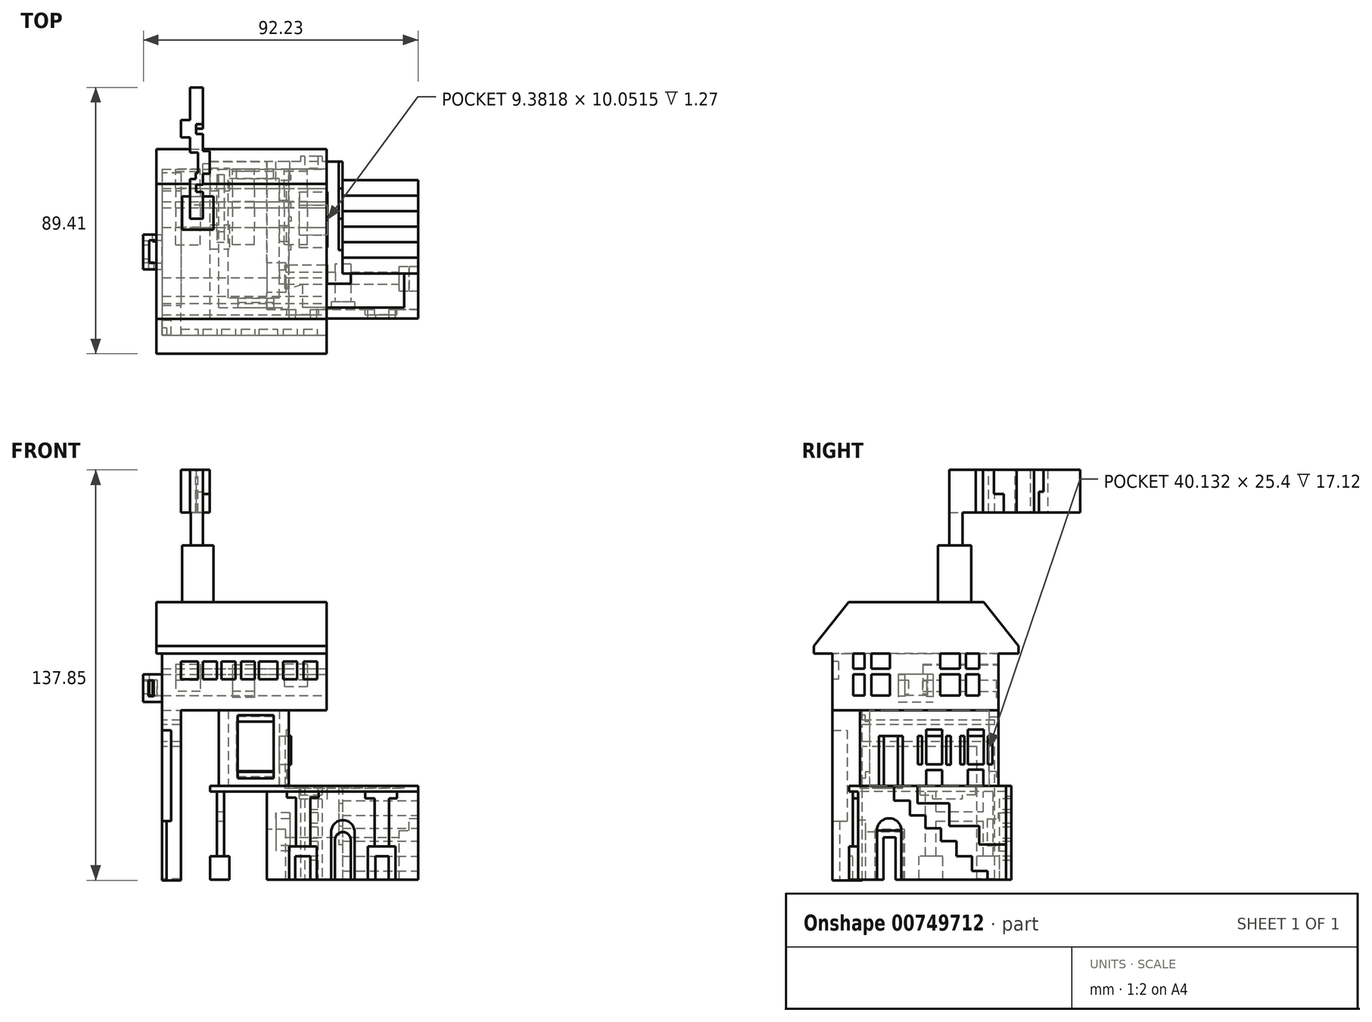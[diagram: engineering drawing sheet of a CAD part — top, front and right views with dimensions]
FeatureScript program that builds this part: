
annotation { "Feature Type Name" : "Feature", "Feature Type Description" : "" }
export const myFeature = defineFeature(function(context is Context, id is Id, definition is map)
    precondition{}
    {
        {
            var Q0;
            Q0=qCreatedBy(makeId("Right.planeOp"),FACE);
            var sketch = newSketch(context, id + "F0", { "sketchPlane" : qUnion([Q0])});
            skLineSegment(sketch, "E0.bottom", {"start": v(-30.5, 23.62) * mm, "end": v(19.16, 23.62) * mm});
            skLineSegment(sketch, "E0.top", {"start": v(-30.5, -7.94) * mm, "end": v(19.16, -7.94) * mm});
            skLineSegment(sketch, "E0.left", {"start": v(-30.5, 23.62) * mm, "end": v(-30.5, -7.94) * mm});
            skLineSegment(sketch, "E0.right", {"start": v(19.16, 23.62) * mm, "end": v(19.16, -7.94) * mm});
            skSolve(sketch);
        }
        {
            var Q0;
            Q0 = qSketchRegion(id + "F0", true);
            extrude(context, id + "F1", {"entities" : qUnion([Q0]), "depth" : 50.8 * mm, "offsetDistance" : 25.4 * mm});
        }
        {
            var Q0;
            Q0=makeQuery(id+"F1.opExtrude","CAP_FACE",FACE,{"disambiguationData":[OSD([sQuery(id+"F0.wireOp",EDGE,"E0.bottom"),sQuery(id+"F0.wireOp",EDGE,"E0.top"),sQuery(id+"F0.wireOp",EDGE,"E0.left"),sQuery(id+"F0.wireOp",EDGE,"E0.right")])],"isStart":false});
            var sketch = newSketch(context, id + "F2", { "sketchPlane" : qUnion([Q0])});
            skLineSegment(sketch, "E1", {"start": v(-18.43, 23.62) * mm, "end": v(-18.43, 18.63) * mm});
            skLineSegment(sketch, "E2", {"start": v(-18.43, 18.63) * mm, "end": v(-13.2, 18.63) * mm});
            skLineSegment(sketch, "E3", {"start": v(-13.2, 18.63) * mm, "end": v(-13.2, 13.64) * mm});
            skLineSegment(sketch, "E4", {"start": v(-13.2, 13.64) * mm, "end": v(-7.98, 13.64) * mm});
            skLineSegment(sketch, "E5", {"start": v(-7.98, 13.64) * mm, "end": v(-7.98, 9.31) * mm});
            skLineSegment(sketch, "E6", {"start": v(-7.98, 9.31) * mm, "end": v(-2.75, 9.31) * mm});
            skLineSegment(sketch, "E7", {"start": v(-2.75, 9.31) * mm, "end": v(-2.75, 5) * mm});
            skLineSegment(sketch, "E8", {"start": v(-2.75, 5) * mm, "end": v(2.48, 5) * mm});
            skLineSegment(sketch, "E9", {"start": v(2.48, 5) * mm, "end": v(2.48, 0) * mm});
            skLineSegment(sketch, "E10", {"start": v(2.48, 0) * mm, "end": v(7.7, 0) * mm});
            skLineSegment(sketch, "E11", {"start": v(7.7, 0) * mm, "end": v(7.7, -5) * mm});
            skLineSegment(sketch, "E12", {"start": v(7.7, -5) * mm, "end": v(12.93, -5) * mm});
            skLineSegment(sketch, "E13", {"start": v(12.93, -5) * mm, "end": v(12.93, -7.94) * mm});
            skLineSegment(sketch, "E14", {"start": v(12.93, -7.94) * mm, "end": v(19.16, -7.94) * mm});
            skSolve(sketch);
        }
        {
            var Q0;
            Q0 = qSketchRegion(id + "F2", true);
            var Q1;
            {var subQ0=sQuery(id+"F2.wireOp",EDGE,"E1");Q1=makeQuery(id+"F2.imprint","IMPRINT",FACE,{"disambiguationData":[TD([[makeQuery(id+"F2.imprint","IMPRINT",EDGE,{"derivedFrom":subQ0}),1.0]])]});}
            extrude(context, id + "F3", {"entities" : qUnion([Q0, Q1]), "operationType" : NewBodyOperationType.REMOVE, "oppositeDirection" : true, "depth" : 25.4 * mm, "offsetDistance" : 25.4 * mm});
        }
        {
            var Q0;
            Q0=makeQuery(id+"F1.opExtrude","CAP_FACE",FACE,{"disambiguationData":[OSD([sQuery(id+"F0.wireOp",EDGE,"E0.bottom"),sQuery(id+"F0.wireOp",EDGE,"E0.top"),sQuery(id+"F0.wireOp",EDGE,"E0.left"),sQuery(id+"F0.wireOp",EDGE,"E0.right")])],"isStart":false});
            var sketch = newSketch(context, id + "F4", { "sketchPlane" : qUnion([Q0])});
            skLineSegment(sketch, "E15.bottom", {"start": v(-24.26, -7.94) * mm, "end": v(-16.02, -7.94) * mm});
            skLineSegment(sketch, "E15.top", {"start": v(-24.26, 8.54) * mm, "end": v(-16.02, 8.54) * mm});
            skLineSegment(sketch, "E15.left", {"start": v(-24.26, -7.94) * mm, "end": v(-24.26, 8.54) * mm});
            skLineSegment(sketch, "E15.right", {"start": v(-16.02, -7.94) * mm, "end": v(-16.02, 8.54) * mm});
            skSolve(sketch);
        }
        {
            var Q0;
            Q0 = qSketchRegion(id + "F4", true);
            extrude(context, id + "F5", {"entities" : qUnion([Q0]), "operationType" : NewBodyOperationType.REMOVE, "oppositeDirection" : true, "depth" : 6.35 * mm, "offsetDistance" : 25.4 * mm});
        }
        {
            var Q0;
            Q0=makeQuery(id+"F5.boolean.opBoolean","COPY",FACE,{"derivedFrom":makeQuery(id+"F5.opExtrude","CAP_FACE",FACE,{"disambiguationData":[OSD([sQuery(id+"F4.wireOp",EDGE,"E15.bottom"),sQuery(id+"F4.wireOp",EDGE,"E15.top"),sQuery(id+"F4.wireOp",EDGE,"E15.left"),sQuery(id+"F4.wireOp",EDGE,"E15.right")])],"isStart":false})});
            var sketch = newSketch(context, id + "F6", { "sketchPlane" : qUnion([Q0])});
            skLineSegment(sketch, "E16.bottom", {"start": v(-22.05, -7.94) * mm, "end": v(-18.03, -7.94) * mm});
            skLineSegment(sketch, "E16.top", {"start": v(-22.05, 6.33) * mm, "end": v(-18.03, 6.33) * mm});
            skLineSegment(sketch, "E16.left", {"start": v(-22.05, -7.94) * mm, "end": v(-22.05, 6.33) * mm});
            skLineSegment(sketch, "E16.right", {"start": v(-18.03, -7.94) * mm, "end": v(-18.03, 6.33) * mm});
            skSolve(sketch);
        }
        {
            var Q0;
            Q0 = qSketchRegion(id + "F6", true);
            extrude(context, id + "F7", {"entities" : qUnion([Q0]), "operationType" : NewBodyOperationType.REMOVE, "endBound" : BoundingType.THROUGH_ALL, "oppositeDirection" : true, "depth" : 25.4 * mm, "offsetDistance" : 25.4 * mm});
        }
        {
            var Q0;
            Q0=makeQuery(id+"F1.opExtrude","CAP_FACE",FACE,{"disambiguationData":[OSD([sQuery(id+"F0.wireOp",EDGE,"E0.bottom"),sQuery(id+"F0.wireOp",EDGE,"E0.top"),sQuery(id+"F0.wireOp",EDGE,"E0.left"),sQuery(id+"F0.wireOp",EDGE,"E0.right")])],"isStart":true});
            var sketch = newSketch(context, id + "F8", { "sketchPlane" : qUnion([Q0])});
            skLineSegment(sketch, "E17.bottom", {"start": v(14.94, -7.94) * mm, "end": v(24.8, -7.94) * mm});
            skLineSegment(sketch, "E17.top", {"start": v(14.94, 8.95) * mm, "end": v(24.8, 8.95) * mm});
            skLineSegment(sketch, "E17.left", {"start": v(14.94, -7.94) * mm, "end": v(14.94, 8.95) * mm});
            skLineSegment(sketch, "E17.right", {"start": v(24.8, -7.94) * mm, "end": v(24.8, 8.95) * mm});
            skSolve(sketch);
        }
        {
            var Q0;
            Q0 = qSketchRegion(id + "F8", true);
            extrude(context, id + "F9", {"entities" : qUnion([Q0]), "operationType" : NewBodyOperationType.REMOVE, "oppositeDirection" : true, "depth" : 6.35 * mm, "offsetDistance" : 25.4 * mm});
        }
        {
            var Q0;
            Q0=makeQuery(id+"F1.opExtrude","SWEPT_FACE",FACE,{"disambiguationData":[OSD([sQuery(id+"F0.wireOp",EDGE,"E0.right")])]});
            var sketch = newSketch(context, id + "F10", { "sketchPlane" : qUnion([Q0])});
            skLineSegment(sketch, "E18.bottom", {"start": v(-18.6, 23.62) * mm, "end": v(-17.2, 23.62) * mm});
            skLineSegment(sketch, "E18.top", {"start": v(-18.6, -7.94) * mm, "end": v(-17.2, -7.94) * mm});
            skLineSegment(sketch, "E18.left", {"start": v(-18.6, 23.62) * mm, "end": v(-18.6, -7.94) * mm});
            skLineSegment(sketch, "E18.right", {"start": v(-17.2, 23.62) * mm, "end": v(-17.2, -7.94) * mm});
            skLineSegment(sketch, "E19.bottom", {"start": v(-12.7, 23.62) * mm, "end": v(-11.3, 23.62) * mm});
            skLineSegment(sketch, "E19.top", {"start": v(-12.7, -7.94) * mm, "end": v(-11.3, -7.94) * mm});
            skLineSegment(sketch, "E19.left", {"start": v(-12.7, 23.62) * mm, "end": v(-12.7, -7.94) * mm});
            skLineSegment(sketch, "E19.right", {"start": v(-11.3, 23.62) * mm, "end": v(-11.3, -7.94) * mm});
            skLineSegment(sketch, "E20.bottom", {"start": v(-17.2, 20) * mm, "end": v(-12.7, 20) * mm});
            skLineSegment(sketch, "E20.top", {"start": v(-17.2, 19.2) * mm, "end": v(-12.7, 19.2) * mm});
            skLineSegment(sketch, "E20.left", {"start": v(-17.2, 20) * mm, "end": v(-17.2, 19.2) * mm});
            skLineSegment(sketch, "E20.right", {"start": v(-12.7, 20) * mm, "end": v(-12.7, 19.2) * mm});
            skLineSegment(sketch, "E21.bottom", {"start": v(-17.2, 15.58) * mm, "end": v(-12.7, 15.58) * mm});
            skLineSegment(sketch, "E21.top", {"start": v(-17.2, 14.57) * mm, "end": v(-12.7, 14.57) * mm});
            skLineSegment(sketch, "E21.left", {"start": v(-17.2, 15.58) * mm, "end": v(-17.2, 14.57) * mm});
            skLineSegment(sketch, "E21.right", {"start": v(-12.7, 15.58) * mm, "end": v(-12.7, 14.57) * mm});
            skLineSegment(sketch, "E22.bottom", {"start": v(-17.2, 10.96) * mm, "end": v(-12.7, 10.96) * mm});
            skLineSegment(sketch, "E22.top", {"start": v(-17.2, 9.75) * mm, "end": v(-12.7, 9.75) * mm});
            skLineSegment(sketch, "E22.left", {"start": v(-17.2, 10.96) * mm, "end": v(-17.2, 9.75) * mm});
            skLineSegment(sketch, "E22.right", {"start": v(-12.7, 10.96) * mm, "end": v(-12.7, 9.75) * mm});
            skLineSegment(sketch, "E23.bottom", {"start": v(-17.2, 5.93) * mm, "end": v(-12.7, 5.93) * mm});
            skLineSegment(sketch, "E23.top", {"start": v(-17.2, 4.93) * mm, "end": v(-12.7, 4.93) * mm});
            skLineSegment(sketch, "E23.left", {"start": v(-17.2, 5.93) * mm, "end": v(-17.2, 4.93) * mm});
            skLineSegment(sketch, "E23.right", {"start": v(-12.7, 5.93) * mm, "end": v(-12.7, 4.93) * mm});
            skLineSegment(sketch, "E24.bottom", {"start": v(-17.2, 0) * mm, "end": v(-12.7, 0) * mm});
            skLineSegment(sketch, "E24.top", {"start": v(-17.2, -1.5) * mm, "end": v(-12.7, -1.5) * mm});
            skLineSegment(sketch, "E24.left", {"start": v(-17.2, 0) * mm, "end": v(-17.2, -1.5) * mm});
            skLineSegment(sketch, "E24.right", {"start": v(-12.7, 0) * mm, "end": v(-12.7, -1.5) * mm});
            skSolve(sketch);
        }
        {
            var Q0;
            Q0 = qSketchRegion(id + "F10", true);
            var Q1;
            Q1=makeQuery(id+"F10.imprint","IMPRINT",FACE,{"disambiguationData":[TD([[makeQuery(id+"F10.imprint","IMPRINT",EDGE,{"derivedFrom":sQuery(id+"F10.wireOp",EDGE,"E23.bottom")}),-1.0]])]});
            var Q2;
            Q2=makeQuery(id+"F10.imprint","IMPRINT",FACE,{"disambiguationData":[TD([[makeQuery(id+"F10.imprint","IMPRINT",EDGE,{"derivedFrom":sQuery(id+"F10.wireOp",EDGE,"E22.bottom")}),-1.0]])]});
            var Q3;
            Q3=makeQuery(id+"F10.imprint","IMPRINT",FACE,{"disambiguationData":[TD([[makeQuery(id+"F10.imprint","IMPRINT",EDGE,{"derivedFrom":sQuery(id+"F10.wireOp",EDGE,"E21.bottom")}),-1.0]])]});
            extrude(context, id + "F11", {"entities" : qUnion([Q0, Q1, Q2, Q3]), "operationType" : NewBodyOperationType.ADD, "depth" : 1.78 * mm, "offsetDistance" : 25.4 * mm});
        }
        {
            var Q0;
            {var subQ0=sQuery(id+"F10.wireOp",EDGE,"E20.top");Q0=makeQuery(id+"F11.boolean.opBoolean","SPLIT",FACE,{"disambiguationData":[TD([makeQuery(id+"F11.opExtrude","SWEPT_FACE",FACE,{"disambiguationData":[OSD([subQ0])]})])],"derivedFrom":makeQuery(id+"F1.opExtrude","SWEPT_FACE",FACE,{"disambiguationData":[OSD([sQuery(id+"F0.wireOp",EDGE,"E0.right")])]})});}
            var Q1;
            {var subQ0=sQuery(id+"F10.wireOp",EDGE,"E21.top");Q1=makeQuery(id+"F11.boolean.opBoolean","SPLIT",FACE,{"disambiguationData":[TD([makeQuery(id+"F11.opExtrude","SWEPT_FACE",FACE,{"disambiguationData":[OSD([subQ0])]})])],"derivedFrom":makeQuery(id+"F1.opExtrude","SWEPT_FACE",FACE,{"disambiguationData":[OSD([sQuery(id+"F0.wireOp",EDGE,"E0.right")])]})});}
            var Q2;
            {var subQ0=sQuery(id+"F10.wireOp",EDGE,"E22.top");Q2=makeQuery(id+"F11.boolean.opBoolean","SPLIT",FACE,{"disambiguationData":[TD([makeQuery(id+"F11.opExtrude","SWEPT_FACE",FACE,{"disambiguationData":[OSD([subQ0])]})])],"derivedFrom":makeQuery(id+"F1.opExtrude","SWEPT_FACE",FACE,{"disambiguationData":[OSD([sQuery(id+"F0.wireOp",EDGE,"E0.right")])]})});}
            var Q3;
            {var subQ0=sQuery(id+"F10.wireOp",EDGE,"E23.top");Q3=makeQuery(id+"F11.boolean.opBoolean","SPLIT",FACE,{"disambiguationData":[TD([makeQuery(id+"F11.opExtrude","SWEPT_FACE",FACE,{"disambiguationData":[OSD([subQ0])]})])],"derivedFrom":makeQuery(id+"F1.opExtrude","SWEPT_FACE",FACE,{"disambiguationData":[OSD([sQuery(id+"F0.wireOp",EDGE,"E0.right")])]})});}
            var Q4;
            {var subQ3=sQuery(id+"F0.wireOp",EDGE,"E0.right");var subQ6=sQuery(id+"F10.wireOp",EDGE,"E24.top");Q4=makeQuery(id+"F11.boolean.opBoolean","SPLIT",FACE,{"disambiguationData":[TD([makeQuery(id+"F11.opExtrude","SWEPT_FACE",FACE,{"disambiguationData":[OSD([subQ6])]})])],"derivedFrom":makeQuery(id+"F1.opExtrude","SWEPT_FACE",FACE,{"disambiguationData":[OSD([subQ3])]})});}
            extrude(context, id + "F12", {"entities" : qUnion([Q0, Q1, Q2, Q3, Q4]), "operationType" : NewBodyOperationType.REMOVE, "oppositeDirection" : true, "depth" : 2.3 * mm, "offsetDistance" : 25.4 * mm});
        }
        {
            var Q0;
            {var subQ1=sQuery(id+"F0.wireOp",EDGE,"E0.right");Q0=makeQuery(id+"F11.boolean.opBoolean","SPLIT",FACE,{"disambiguationData":[TD([makeQuery(id+"F11.opExtrude","SWEPT_FACE",FACE,{"disambiguationData":[OSD([sQuery(id+"F10.wireOp",EDGE,"E19.right")])]})])],"derivedFrom":makeQuery(id+"F1.opExtrude","SWEPT_FACE",FACE,{"disambiguationData":[OSD([subQ1])]})});}
            var sketch = newSketch(context, id + "F13", { "sketchPlane" : qUnion([Q0])});
            skLineSegment(sketch, "E25.bottom", {"start": v(-7.74, 12.56) * mm, "end": v(-3.12, 12.56) * mm});
            skLineSegment(sketch, "E25.top", {"start": v(-7.74, 3.52) * mm, "end": v(-3.12, 3.52) * mm});
            skLineSegment(sketch, "E25.left", {"start": v(-7.74, 12.56) * mm, "end": v(-7.74, 3.52) * mm});
            skLineSegment(sketch, "E25.right", {"start": v(-3.12, 12.56) * mm, "end": v(-3.12, 3.52) * mm});
            skSolve(sketch);
        }
        {
            var Q0;
            Q0 = qSketchRegion(id + "F13", true);
            extrude(context, id + "F14", {"entities" : qUnion([Q0]), "operationType" : NewBodyOperationType.REMOVE, "oppositeDirection" : true, "depth" : 6.35 * mm, "offsetDistance" : 25.4 * mm});
        }
        {
            var Q0;
            {var subQ1=sQuery(id+"F0.wireOp",EDGE,"E0.right");Q0=makeQuery(id+"F11.boolean.opBoolean","SPLIT",FACE,{"disambiguationData":[TD([makeQuery(id+"F11.opExtrude","SWEPT_FACE",FACE,{"disambiguationData":[OSD([sQuery(id+"F10.wireOp",EDGE,"E19.right")])]})])],"derivedFrom":makeQuery(id+"F1.opExtrude","SWEPT_FACE",FACE,{"disambiguationData":[OSD([subQ1])]})});}
            var sketch = newSketch(context, id + "F15", { "sketchPlane" : qUnion([Q0])});
            skLineSegment(sketch, "E26.bottom", {"start": v(-7.74, 12.56) * mm, "end": v(-3.12, 12.56) * mm});
            skLineSegment(sketch, "E26.top", {"start": v(-7.74, 14.57) * mm, "end": v(-3.12, 14.57) * mm});
            skLineSegment(sketch, "E26.left", {"start": v(-7.74, 12.56) * mm, "end": v(-7.74, 14.57) * mm});
            skLineSegment(sketch, "E26.right", {"start": v(-3.12, 12.56) * mm, "end": v(-3.12, 14.57) * mm});
            skLineSegment(sketch, "E27.bottom", {"start": v(-7.74, 3.52) * mm, "end": v(-3.12, 3.52) * mm});
            skLineSegment(sketch, "E27.top", {"start": v(-7.74, 1.7) * mm, "end": v(-3.12, 1.7) * mm});
            skLineSegment(sketch, "E27.left", {"start": v(-7.74, 3.52) * mm, "end": v(-7.74, 1.7) * mm});
            skLineSegment(sketch, "E27.right", {"start": v(-3.12, 3.52) * mm, "end": v(-3.12, 1.7) * mm});
            skSolve(sketch);
        }
        {
            var Q0;
            Q0 = qSketchRegion(id + "F15", true);
            extrude(context, id + "F16", {"entities" : qUnion([Q0]), "operationType" : NewBodyOperationType.REMOVE, "oppositeDirection" : true, "depth" : 2.54 * mm, "offsetDistance" : 25.4 * mm});
        }
        {
            var Q0;
            Q0=makeQuery(id+"F1.opExtrude","SWEPT_FACE",FACE,{"disambiguationData":[OSD([sQuery(id+"F0.wireOp",EDGE,"E0.left")])]});
            var sketch = newSketch(context, id + "F17", { "sketchPlane" : qUnion([Q0])});
            skLineSegment(sketch, "E28.bottom", {"start": v(9.75, 23.62) * mm, "end": v(14.6, 23.62) * mm});
            skLineSegment(sketch, "E28.top", {"start": v(9.75, -7.94) * mm, "end": v(14.6, -7.94) * mm});
            skLineSegment(sketch, "E28.left", {"start": v(9.75, 23.62) * mm, "end": v(9.75, -7.94) * mm});
            skLineSegment(sketch, "E28.right", {"start": v(14.6, 23.62) * mm, "end": v(14.6, -7.94) * mm});
            skLineSegment(sketch, "E29.bottom", {"start": v(7.57, -7.94) * mm, "end": v(16.81, -7.94) * mm});
            skLineSegment(sketch, "E29.top", {"start": v(7.57, 3.31) * mm, "end": v(16.81, 3.31) * mm});
            skLineSegment(sketch, "E29.left", {"start": v(7.57, -7.94) * mm, "end": v(7.57, 3.31) * mm});
            skLineSegment(sketch, "E29.right", {"start": v(16.81, -7.94) * mm, "end": v(16.81, 3.31) * mm});
            skLineSegment(sketch, "E30.bottom", {"start": v(36.2, 23.62) * mm, "end": v(41.05, 23.62) * mm});
            skLineSegment(sketch, "E30.top", {"start": v(36.2, -7.94) * mm, "end": v(41.05, -7.94) * mm});
            skLineSegment(sketch, "E30.left", {"start": v(36.2, 23.62) * mm, "end": v(36.2, -7.94) * mm});
            skLineSegment(sketch, "E30.right", {"start": v(41.05, 23.62) * mm, "end": v(41.05, -7.94) * mm});
            skLineSegment(sketch, "E31.bottom", {"start": v(33.99, -7.94) * mm, "end": v(43.23, -7.94) * mm});
            skLineSegment(sketch, "E31.top", {"start": v(33.99, 3.31) * mm, "end": v(43.23, 3.31) * mm});
            skLineSegment(sketch, "E31.left", {"start": v(33.99, -7.94) * mm, "end": v(33.99, 3.31) * mm});
            skLineSegment(sketch, "E31.right", {"start": v(43.23, -7.94) * mm, "end": v(43.23, 3.31) * mm});
            skLineSegment(sketch, "E32.bottom", {"start": v(0, 23.62) * mm, "end": v(50.8, 23.62) * mm});
            skLineSegment(sketch, "E32.top", {"start": v(0, 21.61) * mm, "end": v(50.8, 21.61) * mm});
            skLineSegment(sketch, "E32.left", {"start": v(0, 23.62) * mm, "end": v(0, 21.61) * mm});
            skLineSegment(sketch, "E32.right", {"start": v(50.8, 23.62) * mm, "end": v(50.8, 21.61) * mm});
            skLineSegment(sketch, "E33.bottom", {"start": v(6.75, 23.62) * mm, "end": v(17.4, 23.62) * mm});
            skLineSegment(sketch, "E33.top", {"start": v(6.75, 19.6) * mm, "end": v(17.4, 19.6) * mm});
            skLineSegment(sketch, "E33.left", {"start": v(6.75, 23.62) * mm, "end": v(6.75, 19.6) * mm});
            skLineSegment(sketch, "E33.right", {"start": v(17.4, 23.62) * mm, "end": v(17.4, 19.6) * mm});
            skLineSegment(sketch, "E34.bottom", {"start": v(33.09, 23.62) * mm, "end": v(43.73, 23.62) * mm});
            skLineSegment(sketch, "E34.top", {"start": v(33.09, 19.4) * mm, "end": v(43.73, 19.4) * mm});
            skLineSegment(sketch, "E34.left", {"start": v(33.09, 23.62) * mm, "end": v(33.09, 19.4) * mm});
            skLineSegment(sketch, "E34.right", {"start": v(43.73, 23.62) * mm, "end": v(43.73, 19.4) * mm});
            skSolve(sketch);
        }
        {
            var Q0;
            Q0 = qSketchRegion(id + "F17", true);
            extrude(context, id + "F18", {"entities" : qUnion([Q0]), "operationType" : NewBodyOperationType.ADD, "depth" : 3.05 * mm, "offsetDistance" : 25.4 * mm});
        }
        {
            var Q0;
            Q0=makeQuery(id+"F18.opExtrude","CAP_FACE",FACE,{"disambiguationData":[OSD([sQuery(id+"F17.wireOp",EDGE,"E28.left"),sQuery(id+"F17.wireOp",EDGE,"E28.right"),sQuery(id+"F17.wireOp",EDGE,"E29.bottom"),sQuery(id+"F17.wireOp",EDGE,"E29.top"),sQuery(id+"F17.wireOp",EDGE,"E29.left"),sQuery(id+"F17.wireOp",EDGE,"E29.right"),sQuery(id+"F17.wireOp",EDGE,"E30.left"),sQuery(id+"F17.wireOp",EDGE,"E30.right"),sQuery(id+"F17.wireOp",EDGE,"E31.bottom"),sQuery(id+"F17.wireOp",EDGE,"E31.top"),sQuery(id+"F17.wireOp",EDGE,"E31.left"),sQuery(id+"F17.wireOp",EDGE,"E31.right"),sQuery(id+"F17.wireOp",EDGE,"E32.bottom"),sQuery(id+"F17.wireOp",EDGE,"E32.top"),sQuery(id+"F17.wireOp",EDGE,"E32.left"),sQuery(id+"F17.wireOp",EDGE,"E32.right"),sQuery(id+"F17.wireOp",EDGE,"E33.bottom"),sQuery(id+"F17.wireOp",EDGE,"E33.top"),sQuery(id+"F17.wireOp",EDGE,"E33.left"),sQuery(id+"F17.wireOp",EDGE,"E33.right"),sQuery(id+"F17.wireOp",EDGE,"E34.bottom"),sQuery(id+"F17.wireOp",EDGE,"E34.top"),sQuery(id+"F17.wireOp",EDGE,"E34.left"),sQuery(id+"F17.wireOp",EDGE,"E34.right")])],"isStart":false});
            var sketch = newSketch(context, id + "F19", { "sketchPlane" : qUnion([Q0])});
            skLineSegment(sketch, "E35", {"start": v(6.75, 21.61) * mm, "end": v(17.4, 21.61) * mm});
            skLineSegment(sketch, "E36", {"start": v(33.09, 21.61) * mm, "end": v(43.73, 21.61) * mm});
            skLineSegment(sketch, "E37", {"start": v(9.75, 3.31) * mm, "end": v(14.6, 3.31) * mm});
            skLineSegment(sketch, "E38", {"start": v(36.2, 3.31) * mm, "end": v(41.05, 3.31) * mm});
            skSolve(sketch);
        }
        {
            var Q0;
            Q0 = qSketchRegion(id + "F19", true);
            var Q1;
            Q1=makeQuery(id+"F19.imprint","IMPRINT",FACE,{"disambiguationData":[TD([[makeQuery(id+"F19.imprint","IMPRINT",EDGE,{"derivedFrom":sQuery(id+"F19.wireOp",EDGE,"E35")}),-1.0]])]});
            var Q2;
            Q2=makeQuery(id+"F19.imprint","IMPRINT",FACE,{"disambiguationData":[TD([[makeQuery(id+"F19.imprint","IMPRINT",EDGE,{"derivedFrom":sQuery(id+"F19.wireOp",EDGE,"E36")}),-1.0]])]});
            extrude(context, id + "F20", {"entities" : qUnion([Q0, Q1, Q2]), "operationType" : NewBodyOperationType.REMOVE, "oppositeDirection" : true, "depth" : 1.27 * mm, "offsetDistance" : 25.4 * mm});
        }
        {
            var Q0;
            {var subQ0=sQuery(id+"F17.wireOp",EDGE,"E29.right");var subQ1=sQuery(id+"F17.wireOp",EDGE,"E29.top");var subQ2=sQuery(id+"F17.wireOp",EDGE,"E28.right");var subQ3=sQuery(id+"F17.wireOp",EDGE,"E29.bottom");var subQ4=sQuery(id+"F17.wireOp",EDGE,"E29.left");var subQ5=sQuery(id+"F17.wireOp",EDGE,"E28.left");var subQ6=sQuery(id+"F17.wireOp",EDGE,"E31.bottom");Q0=makeQuery(id+"F20.boolean.opBoolean","SPLIT",FACE,{"disambiguationData":[TD([makeQuery(id+"F18.opExtrude","SWEPT_FACE",FACE,{"disambiguationData":[OSD([subQ4])]})])],"derivedFrom":makeQuery(id+"F18.opExtrude","CAP_FACE",FACE,{"disambiguationData":[OSD([subQ5,subQ2,subQ3,subQ1,subQ4,subQ0,sQuery(id+"F17.wireOp",EDGE,"E30.left"),sQuery(id+"F17.wireOp",EDGE,"E30.right"),subQ6,sQuery(id+"F17.wireOp",EDGE,"E31.top"),sQuery(id+"F17.wireOp",EDGE,"E31.left"),sQuery(id+"F17.wireOp",EDGE,"E31.right"),sQuery(id+"F17.wireOp",EDGE,"E32.bottom"),sQuery(id+"F17.wireOp",EDGE,"E32.top"),sQuery(id+"F17.wireOp",EDGE,"E32.left"),sQuery(id+"F17.wireOp",EDGE,"E32.right"),sQuery(id+"F17.wireOp",EDGE,"E33.bottom"),sQuery(id+"F17.wireOp",EDGE,"E33.top"),sQuery(id+"F17.wireOp",EDGE,"E33.left"),sQuery(id+"F17.wireOp",EDGE,"E33.right"),sQuery(id+"F17.wireOp",EDGE,"E34.bottom"),sQuery(id+"F17.wireOp",EDGE,"E34.top"),sQuery(id+"F17.wireOp",EDGE,"E34.left"),sQuery(id+"F17.wireOp",EDGE,"E34.right")])],"isStart":false})});}
            var sketch = newSketch(context, id + "F21", { "sketchPlane" : qUnion([Q0])});
            skLineSegment(sketch, "E39.bottom", {"start": v(9.57, -7.94) * mm, "end": v(14.6, -7.94) * mm});
            skLineSegment(sketch, "E39.top", {"start": v(9.57, 0) * mm, "end": v(14.6, 0) * mm});
            skLineSegment(sketch, "E39.left", {"start": v(9.57, -7.94) * mm, "end": v(9.57, 0) * mm});
            skLineSegment(sketch, "E39.right", {"start": v(14.6, -7.94) * mm, "end": v(14.6, 0) * mm});
            skSolve(sketch);
        }
        {
            var Q0;
            Q0 = qSketchRegion(id + "F21", true);
            extrude(context, id + "F22", {"entities" : qUnion([Q0]), "operationType" : NewBodyOperationType.REMOVE, "oppositeDirection" : true, "depth" : 1.27 * mm, "offsetDistance" : 25.4 * mm});
        }
        {
            var Q0;
            {var subQ0=sQuery(id+"F17.wireOp",EDGE,"E31.left");var subQ1=sQuery(id+"F17.wireOp",EDGE,"E31.top");var subQ2=sQuery(id+"F17.wireOp",EDGE,"E30.left");var subQ3=sQuery(id+"F17.wireOp",EDGE,"E31.bottom");var subQ4=sQuery(id+"F17.wireOp",EDGE,"E29.bottom");var subQ5=sQuery(id+"F17.wireOp",EDGE,"E31.right");var subQ6=sQuery(id+"F17.wireOp",EDGE,"E30.right");Q0=makeQuery(id+"F20.boolean.opBoolean","SPLIT",FACE,{"disambiguationData":[TD([makeQuery(id+"F18.opExtrude","SWEPT_FACE",FACE,{"disambiguationData":[OSD([subQ0])]})])],"derivedFrom":makeQuery(id+"F18.opExtrude","CAP_FACE",FACE,{"disambiguationData":[OSD([sQuery(id+"F17.wireOp",EDGE,"E28.left"),sQuery(id+"F17.wireOp",EDGE,"E28.right"),subQ4,sQuery(id+"F17.wireOp",EDGE,"E29.top"),sQuery(id+"F17.wireOp",EDGE,"E29.left"),sQuery(id+"F17.wireOp",EDGE,"E29.right"),subQ2,subQ6,subQ3,subQ1,subQ0,subQ5,sQuery(id+"F17.wireOp",EDGE,"E32.bottom"),sQuery(id+"F17.wireOp",EDGE,"E32.top"),sQuery(id+"F17.wireOp",EDGE,"E32.left"),sQuery(id+"F17.wireOp",EDGE,"E32.right"),sQuery(id+"F17.wireOp",EDGE,"E33.bottom"),sQuery(id+"F17.wireOp",EDGE,"E33.top"),sQuery(id+"F17.wireOp",EDGE,"E33.left"),sQuery(id+"F17.wireOp",EDGE,"E33.right"),sQuery(id+"F17.wireOp",EDGE,"E34.bottom"),sQuery(id+"F17.wireOp",EDGE,"E34.top"),sQuery(id+"F17.wireOp",EDGE,"E34.left"),sQuery(id+"F17.wireOp",EDGE,"E34.right")])],"isStart":false})});}
            var sketch = newSketch(context, id + "F23", { "sketchPlane" : qUnion([Q0])});
            skLineSegment(sketch, "E40.bottom", {"start": v(36.5, -7.94) * mm, "end": v(40.93, -7.94) * mm});
            skLineSegment(sketch, "E40.top", {"start": v(36.5, 0) * mm, "end": v(40.93, 0) * mm});
            skLineSegment(sketch, "E40.left", {"start": v(36.5, -7.94) * mm, "end": v(36.5, 0) * mm});
            skLineSegment(sketch, "E40.right", {"start": v(40.93, -7.94) * mm, "end": v(40.93, 0) * mm});
            skSolve(sketch);
        }
        {
            var Q0;
            Q0 = qSketchRegion(id + "F23", true);
            extrude(context, id + "F24", {"entities" : qUnion([Q0]), "operationType" : NewBodyOperationType.REMOVE, "oppositeDirection" : true, "depth" : 1.27 * mm, "offsetDistance" : 25.4 * mm});
        }
        {
            var Q0;
            Q0=makeQuery(id+"F18.boolean.opBoolean","MERGE",FACE,{"derivedFrom":[makeQuery(id+"F1.opExtrude","CAP_FACE",FACE,{"disambiguationData":[OSD([sQuery(id+"F0.wireOp",EDGE,"E0.bottom"),sQuery(id+"F0.wireOp",EDGE,"E0.top"),sQuery(id+"F0.wireOp",EDGE,"E0.left"),sQuery(id+"F0.wireOp",EDGE,"E0.right")])],"isStart":true}),makeQuery(id+"F18.opExtrude","SWEPT_FACE",FACE,{"disambiguationData":[OSD([sQuery(id+"F17.wireOp",EDGE,"E32.left")])]})]});
            var sketch = newSketch(context, id + "F25", { "sketchPlane" : qUnion([Q0])});
            skLineSegment(sketch, "E41.bottom", {"start": v(-14.76, 23.62) * mm, "end": v(-11.54, 23.62) * mm});
            skLineSegment(sketch, "E41.top", {"start": v(-14.76, -7.94) * mm, "end": v(-11.54, -7.94) * mm});
            skLineSegment(sketch, "E41.left", {"start": v(-14.76, 23.62) * mm, "end": v(-14.76, -7.94) * mm});
            skLineSegment(sketch, "E41.right", {"start": v(-11.54, 23.62) * mm, "end": v(-11.54, -7.94) * mm});
            skLineSegment(sketch, "E42.bottom", {"start": v(4.34, 23.62) * mm, "end": v(7.96, 23.62) * mm});
            skLineSegment(sketch, "E42.top", {"start": v(4.34, -7.94) * mm, "end": v(7.96, -7.94) * mm});
            skLineSegment(sketch, "E42.left", {"start": v(4.34, 23.62) * mm, "end": v(4.34, -7.94) * mm});
            skLineSegment(sketch, "E42.right", {"start": v(7.96, 23.62) * mm, "end": v(7.96, -7.94) * mm});
            skLineSegment(sketch, "E43.bottom", {"start": v(-14.76, 14.98) * mm, "end": v(7.96, 14.98) * mm});
            skLineSegment(sketch, "E43.top", {"start": v(-14.76, 11.76) * mm, "end": v(7.96, 11.76) * mm});
            skLineSegment(sketch, "E43.left", {"start": v(-14.76, 14.98) * mm, "end": v(-14.76, 11.76) * mm});
            skLineSegment(sketch, "E43.right", {"start": v(7.96, 14.98) * mm, "end": v(7.96, 11.76) * mm});
            skLineSegment(sketch, "E44.bottom", {"start": v(-19.16, 23.62) * mm, "end": v(33.54, 23.62) * mm});
            skLineSegment(sketch, "E44.top", {"start": v(-19.16, 21.61) * mm, "end": v(33.54, 21.61) * mm});
            skLineSegment(sketch, "E44.left", {"start": v(-19.16, 23.62) * mm, "end": v(-19.16, 21.61) * mm});
            skLineSegment(sketch, "E44.right", {"start": v(33.54, 23.62) * mm, "end": v(33.54, 21.61) * mm});
            skLineSegment(sketch, "E45.bottom", {"start": v(-16.97, -7.94) * mm, "end": v(-9.33, -7.94) * mm});
            skLineSegment(sketch, "E45.top", {"start": v(-16.97, 0) * mm, "end": v(-9.33, 0) * mm});
            skLineSegment(sketch, "E45.left", {"start": v(-16.97, -7.94) * mm, "end": v(-16.97, 0) * mm});
            skLineSegment(sketch, "E45.right", {"start": v(-9.33, -7.94) * mm, "end": v(-9.33, 0) * mm});
            skLineSegment(sketch, "E46.bottom", {"start": v(2.13, -7.94) * mm, "end": v(10.17, -7.94) * mm});
            skLineSegment(sketch, "E46.top", {"start": v(2.13, 0) * mm, "end": v(10.17, 0) * mm});
            skLineSegment(sketch, "E46.left", {"start": v(2.13, -7.94) * mm, "end": v(2.13, 0) * mm});
            skLineSegment(sketch, "E46.right", {"start": v(10.17, -7.94) * mm, "end": v(10.17, 0) * mm});
            skSolve(sketch);
        }
        {
            var Q0;
            Q0 = qSketchRegion(id + "F25", true);
            extrude(context, id + "F26", {"entities" : qUnion([Q0]), "operationType" : NewBodyOperationType.ADD, "depth" : 19.05 * mm, "offsetDistance" : 25.4 * mm});
        }
        {
            var Q0;
            Q0=makeQuery(id+"F26.opExtrude","SWEPT_FACE",FACE,{"disambiguationData":[OSD([sQuery(id+"F25.wireOp",EDGE,"E42.right"),sQuery(id+"F25.wireOp",EDGE,"E43.right")])]});
            var sketch = newSketch(context, id + "F27", { "sketchPlane" : qUnion([Q0])});
            skLineSegment(sketch, "E47", {"start": v(-14.35, 21.61) * mm, "end": v(-14.35, 0) * mm});
            skSolve(sketch);
        }
        {
            var Q0;
            Q0 = qSketchRegion(id + "F27", true);
            var Q1;
            {var subQ0=sQuery(id+"F27.wireOp",EDGE,"E47");Q1=makeQuery(id+"F27.imprint","IMPRINT",FACE,{"disambiguationData":[TD([[makeQuery(id+"F27.imprint","IMPRINT",EDGE,{"derivedFrom":subQ0}),1.0]])]});}
            extrude(context, id + "F28", {"entities" : qUnion([Q0, Q1]), "operationType" : NewBodyOperationType.REMOVE, "endBound" : BoundingType.THROUGH_ALL, "oppositeDirection" : true, "depth" : 25.4 * mm, "offsetDistance" : 25.4 * mm});
        }
        {
            var Q0;
            Q0=makeQuery(id+"F26.opExtrude","SWEPT_FACE",FACE,{"disambiguationData":[OSD([sQuery(id+"F25.wireOp",EDGE,"E46.right")])]});
            var sketch = newSketch(context, id + "F29", { "sketchPlane" : qUnion([Q0])});
            skLineSegment(sketch, "E48", {"start": v(-12.54, 0) * mm, "end": v(-12.54, -7.94) * mm});
            skSolve(sketch);
        }
        {
            var Q0;
            Q0 = qSketchRegion(id + "F29", true);
            var Q1;
            {var subQ0=sQuery(id+"F29.wireOp",EDGE,"E48");Q1=makeQuery(id+"F29.imprint","IMPRINT",FACE,{"disambiguationData":[TD([[makeQuery(id+"F29.imprint","IMPRINT",EDGE,{"derivedFrom":subQ0}),1.0]])]});}
            extrude(context, id + "F30", {"entities" : qUnion([Q0, Q1]), "operationType" : NewBodyOperationType.REMOVE, "endBound" : BoundingType.THROUGH_ALL, "oppositeDirection" : true, "depth" : 25.4 * mm, "offsetDistance" : 25.4 * mm});
        }
        {
            var Q0;
            Q0=makeQuery(id+"F26.opExtrude","SWEPT_FACE",FACE,{"disambiguationData":[OSD([sQuery(id+"F25.wireOp",EDGE,"E42.right"),sQuery(id+"F25.wireOp",EDGE,"E43.right")])]});
            var sketch = newSketch(context, id + "F31", { "sketchPlane" : qUnion([Q0])});
            skLineSegment(sketch, "E49", {"start": v(-16.7, 0) * mm, "end": v(-16.7, 21.61) * mm});
            skSolve(sketch);
        }
        {
            var Q0;
            Q0 = qSketchRegion(id + "F31", true);
            var Q1;
            {var subQ0=sQuery(id+"F31.wireOp",EDGE,"E49");Q1=makeQuery(id+"F31.imprint","IMPRINT",FACE,{"disambiguationData":[TD([[makeQuery(id+"F31.imprint","IMPRINT",EDGE,{"derivedFrom":subQ0}),1.0]])]});}
            extrude(context, id + "F32", {"entities" : qUnion([Q0, Q1]), "operationType" : NewBodyOperationType.REMOVE, "endBound" : BoundingType.THROUGH_ALL, "oppositeDirection" : true, "depth" : 25.4 * mm, "offsetDistance" : 25.4 * mm});
        }
        {
            var Q0;
            {var subQ7=sQuery(id+"F17.wireOp",EDGE,"E28.right");Q0=makeQuery(id+"F18.boolean.opBoolean","SPLIT",FACE,{"disambiguationData":[TD([makeQuery(id+"F18.opExtrude","SWEPT_FACE",FACE,{"disambiguationData":[OSD([subQ7])]})])],"derivedFrom":makeQuery(id+"F1.opExtrude","SWEPT_FACE",FACE,{"disambiguationData":[OSD([sQuery(id+"F0.wireOp",EDGE,"E0.left")])]})});}
            var sketch = newSketch(context, id + "F33", { "sketchPlane" : qUnion([Q0])});
            skLineSegment(sketch, "E50", {"start": v(21.65, -7.94) * mm, "end": v(21.65, 8.14) * mm});
            skLineSegment(sketch, "E51", {"start": v(21.65, 8.14) * mm, "end": v(29.47, 8.14) * mm});
            skLineSegment(sketch, "E52", {"start": v(29.47, 8.14) * mm, "end": v(29.47, -7.94) * mm});
            skLineSegment(sketch, "E53.left", {"start": v(17.85, 13.09) * mm, "end": v(17.85, 11.48) * mm});
            skLineSegment(sketch, "E53.right", {"start": v(33.63, 13.09) * mm, "end": v(33.63, 11.48) * mm});
            skArc(sketch, "E54", {"start": v(29.47, 8.14) * mm, "mid": v(25.56, 12.05) * mm, "end": v(21.65, 8.14) * mm});
            skSolve(sketch);
        }
        {
            var Q0;
            {var subQ0=sQuery(id+"F33.wireOp",EDGE,"E50");Q0=makeQuery(id+"F33.imprint","IMPRINT",FACE,{"disambiguationData":[TD([[makeQuery(id+"F33.imprint","IMPRINT",EDGE,{"derivedFrom":subQ0}),-1.0]])]});}
            var Q1;
            Q1=makeQuery(id+"F33.imprint","IMPRINT",FACE,{"disambiguationData":[TD([[makeQuery(id+"F33.imprint","IMPRINT",EDGE,{"derivedFrom":sQuery(id+"F33.wireOp",EDGE,"E51")}),1.0]])]});
            extrude(context, id + "F34", {"entities" : qUnion([Q0, Q1]), "operationType" : NewBodyOperationType.REMOVE, "oppositeDirection" : true, "depth" : 2.54 * mm, "offsetDistance" : 25.4 * mm});
        }
        {
            var Q0;
            Q0=makeQuery(id+"F34.boolean.opBoolean","COPY",FACE,{"derivedFrom":makeQuery(id+"F34.opExtrude","CAP_FACE",FACE,{"disambiguationData":[OSD([sQuery(id+"F0.wireOp",EDGE,"E0.top"),sQuery(id+"F0.wireOp",EDGE,"E0.left"),sQuery(id+"F33.wireOp",EDGE,"E50"),sQuery(id+"F33.wireOp",EDGE,"E52"),sQuery(id+"F33.wireOp",EDGE,"E54")])],"isStart":false})});
            var sketch = newSketch(context, id + "F35", { "sketchPlane" : qUnion([Q0])});
            skLineSegment(sketch, "E55.bottom", {"start": v(22.92, -7.94) * mm, "end": v(28.2, -7.94) * mm});
            skLineSegment(sketch, "E55.top", {"start": v(22.92, 5.43) * mm, "end": v(28.2, 5.43) * mm});
            skLineSegment(sketch, "E55.left", {"start": v(22.92, -7.94) * mm, "end": v(22.92, 5.43) * mm});
            skLineSegment(sketch, "E55.right", {"start": v(28.2, -7.94) * mm, "end": v(28.2, 5.43) * mm});
            skArc(sketch, "E56", {"start": v(28.2, 5.43) * mm, "mid": v(25.56, 8.07) * mm, "end": v(22.92, 5.43) * mm});
            skSolve(sketch);
        }
        {
            var Q0;
            Q0 = qSketchRegion(id + "F35", true);
            extrude(context, id + "F36", {"entities" : qUnion([Q0]), "operationType" : NewBodyOperationType.REMOVE, "oppositeDirection" : true, "depth" : 12.7 * mm, "offsetDistance" : 25.4 * mm});
        }
        {
            var Q0;
            Q0=makeQuery(id+"F3.boolean.opBoolean","COPY",FACE,{"derivedFrom":makeQuery(id+"F3.opExtrude","CAP_FACE",FACE,{"disambiguationData":[OSD([sQuery(id+"F0.wireOp",EDGE,"E0.bottom"),sQuery(id+"F0.wireOp",EDGE,"E0.right"),sQuery(id+"F2.wireOp",EDGE,"E1"),sQuery(id+"F2.wireOp",EDGE,"E2"),sQuery(id+"F2.wireOp",EDGE,"E3"),sQuery(id+"F2.wireOp",EDGE,"E4"),sQuery(id+"F2.wireOp",EDGE,"E5"),sQuery(id+"F2.wireOp",EDGE,"E6"),sQuery(id+"F2.wireOp",EDGE,"E7"),sQuery(id+"F2.wireOp",EDGE,"E8"),sQuery(id+"F2.wireOp",EDGE,"E9"),sQuery(id+"F2.wireOp",EDGE,"E10"),sQuery(id+"F2.wireOp",EDGE,"E11"),sQuery(id+"F2.wireOp",EDGE,"E12"),sQuery(id+"F2.wireOp",EDGE,"E13"),sQuery(id+"F2.wireOp",EDGE,"E14")])],"isStart":false})});
            var sketch = newSketch(context, id + "F37", { "sketchPlane" : qUnion([Q0])});
            skLineSegment(sketch, "E57", {"start": v(-10.58, 23.62) * mm, "end": v(-10.58, 17.78) * mm});
            skLineSegment(sketch, "E58", {"start": v(-10.58, 17.78) * mm, "end": v(0, 17.78) * mm});
            skLineSegment(sketch, "E59", {"start": v(0, 17.78) * mm, "end": v(0, 10.16) * mm});
            skLineSegment(sketch, "E60", {"start": v(0, 10.16) * mm, "end": v(10.12, 10.16) * mm});
            skLineSegment(sketch, "E61", {"start": v(10.12, 10.16) * mm, "end": v(10.12, 3.94) * mm});
            skLineSegment(sketch, "E62", {"start": v(10.12, 3.94) * mm, "end": v(19.16, 3.94) * mm});
            skSolve(sketch);
        }
        {
            var Q0;
            Q0 = qSketchRegion(id + "F37", true);
            var Q1;
            {var subQ0=sQuery(id+"F37.wireOp",EDGE,"E57");Q1=makeQuery(id+"F37.imprint","IMPRINT",FACE,{"disambiguationData":[TD([[makeQuery(id+"F37.imprint","IMPRINT",EDGE,{"derivedFrom":subQ0}),1.0]])]});}
            extrude(context, id + "F38", {"entities" : qUnion([Q0, Q1]), "operationType" : NewBodyOperationType.REMOVE, "oppositeDirection" : true, "depth" : 1.27 * mm, "offsetDistance" : 25.4 * mm});
        }
        {
            var Q0;
            Q0=makeQuery(id+"F26.boolean.opBoolean","MERGE",FACE,{"derivedFrom":[makeQuery(id+"F18.boolean.opBoolean","MERGE",FACE,{"derivedFrom":[makeQuery(id+"F11.boolean.opBoolean","MERGE",FACE,{"derivedFrom":[makeQuery(id+"F1.opExtrude","SWEPT_FACE",FACE,{"disambiguationData":[OSD([sQuery(id+"F0.wireOp",EDGE,"E0.bottom")])]}),makeQuery(id+"F11.opExtrude","SWEPT_FACE",FACE,{"disambiguationData":[OSD([sQuery(id+"F10.wireOp",EDGE,"E18.bottom")])]}),makeQuery(id+"F11.opExtrude","SWEPT_FACE",FACE,{"disambiguationData":[OSD([sQuery(id+"F10.wireOp",EDGE,"E19.bottom")])]})]}),makeQuery(id+"F18.opExtrude","SWEPT_FACE",FACE,{"disambiguationData":[OSD([sQuery(id+"F17.wireOp",EDGE,"E32.bottom"),sQuery(id+"F17.wireOp",EDGE,"E33.bottom"),sQuery(id+"F17.wireOp",EDGE,"E34.bottom")])]})]}),makeQuery(id+"F26.opExtrude","SWEPT_FACE",FACE,{"disambiguationData":[OSD([sQuery(id+"F25.wireOp",EDGE,"E44.bottom")])]})]});
            var sketch = newSketch(context, id + "F39", { "sketchPlane" : qUnion([Q0])});
            skLineSegment(sketch, "E63.bottom", {"start": v(4.26, -29.9) * mm, "end": v(7.43, -29.9) * mm});
            skLineSegment(sketch, "E63.top", {"start": v(4.26, 16.58) * mm, "end": v(7.43, 16.58) * mm});
            skLineSegment(sketch, "E63.left", {"start": v(4.26, -29.9) * mm, "end": v(4.26, 16.58) * mm});
            skLineSegment(sketch, "E63.right", {"start": v(7.43, -29.9) * mm, "end": v(7.43, 16.58) * mm});
            skLineSegment(sketch, "E64.bottom", {"start": v(-16.03, -29.9) * mm, "end": v(-12.86, -29.9) * mm});
            skLineSegment(sketch, "E64.top", {"start": v(-16.03, 16.58) * mm, "end": v(-12.86, 16.58) * mm});
            skLineSegment(sketch, "E64.left", {"start": v(-16.03, -29.9) * mm, "end": v(-16.03, 16.58) * mm});
            skLineSegment(sketch, "E64.right", {"start": v(-12.86, -29.9) * mm, "end": v(-12.86, 16.58) * mm});
            skLineSegment(sketch, "E65.bottom", {"start": v(4.26, -29.9) * mm, "end": v(-12.86, -29.9) * mm});
            skLineSegment(sketch, "E65.top", {"start": v(4.26, -26.73) * mm, "end": v(-12.86, -26.73) * mm});
            skLineSegment(sketch, "E65.left", {"start": v(4.26, -29.9) * mm, "end": v(4.26, -26.73) * mm});
            skLineSegment(sketch, "E65.right", {"start": v(-12.86, -29.9) * mm, "end": v(-12.86, -26.73) * mm});
            skLineSegment(sketch, "E66.bottom", {"start": v(4.26, 16.58) * mm, "end": v(-12.86, 16.58) * mm});
            skLineSegment(sketch, "E66.top", {"start": v(4.26, 13.4) * mm, "end": v(-12.86, 13.4) * mm});
            skLineSegment(sketch, "E66.left", {"start": v(4.26, 16.58) * mm, "end": v(4.26, 13.4) * mm});
            skLineSegment(sketch, "E66.right", {"start": v(-12.86, 16.58) * mm, "end": v(-12.86, 13.4) * mm});
            skSolve(sketch);
        }
        {
            var Q0;
            Q0 = qSketchRegion(id + "F39", true);
            extrude(context, id + "F40", {"entities" : qUnion([Q0]), "operationType" : NewBodyOperationType.ADD, "depth" : 25.4 * mm, "offsetDistance" : 25.4 * mm});
        }
        {
            var Q0;
            Q0=makeQuery(id+"F40.opExtrude","SWEPT_FACE",FACE,{"disambiguationData":[OSD([sQuery(id+"F39.wireOp",EDGE,"E63.right")])]});
            var sketch = newSketch(context, id + "F41", { "sketchPlane" : qUnion([Q0])});
            skLineSegment(sketch, "E67.bottom", {"start": v(-23.52, 23.62) * mm, "end": v(-15.6, 23.62) * mm});
            skLineSegment(sketch, "E67.top", {"start": v(-23.52, 40.36) * mm, "end": v(-15.6, 40.36) * mm});
            skLineSegment(sketch, "E67.left", {"start": v(-23.52, 23.62) * mm, "end": v(-23.52, 40.36) * mm});
            skLineSegment(sketch, "E67.right", {"start": v(-15.6, 23.62) * mm, "end": v(-15.6, 40.36) * mm});
            skLineSegment(sketch, "E68.bottom", {"start": v(-7.68, 40.36) * mm, "end": v(-2.3, 40.36) * mm});
            skLineSegment(sketch, "E68.top", {"start": v(-7.68, 30.83) * mm, "end": v(-2.3, 30.83) * mm});
            skLineSegment(sketch, "E68.left", {"start": v(-7.68, 40.36) * mm, "end": v(-7.68, 30.83) * mm});
            skLineSegment(sketch, "E68.right", {"start": v(-2.3, 40.36) * mm, "end": v(-2.3, 30.83) * mm});
            skLineSegment(sketch, "E69.bottom", {"start": v(6.22, 40.36) * mm, "end": v(11.61, 40.36) * mm});
            skLineSegment(sketch, "E69.top", {"start": v(6.22, 30.83) * mm, "end": v(11.61, 30.83) * mm});
            skLineSegment(sketch, "E69.left", {"start": v(6.22, 40.36) * mm, "end": v(6.22, 30.83) * mm});
            skLineSegment(sketch, "E69.right", {"start": v(11.61, 40.36) * mm, "end": v(11.61, 30.83) * mm});
            skSolve(sketch);
        }
        {
            var Q0;
            Q0 = qSketchRegion(id + "F41", true);
            extrude(context, id + "F42", {"entities" : qUnion([Q0]), "operationType" : NewBodyOperationType.REMOVE, "oppositeDirection" : true, "depth" : 1.27 * mm, "offsetDistance" : 25.4 * mm});
        }
        {
            var Q0;
            Q0=makeQuery(id+"F42.boolean.opBoolean","COPY",FACE,{"derivedFrom":makeQuery(id+"F42.opExtrude","CAP_FACE",FACE,{"disambiguationData":[OSD([sQuery(id+"F41.wireOp",EDGE,"E68.bottom"),sQuery(id+"F41.wireOp",EDGE,"E68.top"),sQuery(id+"F41.wireOp",EDGE,"E68.left"),sQuery(id+"F41.wireOp",EDGE,"E68.right")])],"isStart":false})});
            extrude(context, id + "F43", {"entities" : qUnion([Q0]), "operationType" : NewBodyOperationType.REMOVE, "oppositeDirection" : true, "depth" : 4.57 * mm, "offsetDistance" : 25.4 * mm});
        }
        {
            var Q0;
            Q0=makeQuery(id+"F42.boolean.opBoolean","COPY",FACE,{"derivedFrom":makeQuery(id+"F42.opExtrude","CAP_FACE",FACE,{"disambiguationData":[OSD([sQuery(id+"F41.wireOp",EDGE,"E69.bottom"),sQuery(id+"F41.wireOp",EDGE,"E69.top"),sQuery(id+"F41.wireOp",EDGE,"E69.left"),sQuery(id+"F41.wireOp",EDGE,"E69.right")])],"isStart":false})});
            extrude(context, id + "F44", {"entities" : qUnion([Q0]), "operationType" : NewBodyOperationType.REMOVE, "oppositeDirection" : true, "depth" : 4.57 * mm, "offsetDistance" : 25.4 * mm});
        }
        {
            var Q0;
            Q0=makeQuery(id+"F40.opExtrude","SWEPT_FACE",FACE,{"disambiguationData":[OSD([sQuery(id+"F39.wireOp",EDGE,"E63.right")])]});
            var sketch = newSketch(context, id + "F45", { "sketchPlane" : qUnion([Q0])});
            skLineSegment(sketch, "E70.bottom", {"start": v(-10.55, 40.36) * mm, "end": v(-9.05, 40.36) * mm});
            skLineSegment(sketch, "E70.top", {"start": v(-10.55, 30.83) * mm, "end": v(-9.05, 30.83) * mm});
            skLineSegment(sketch, "E70.left", {"start": v(-10.55, 40.36) * mm, "end": v(-10.55, 30.83) * mm});
            skLineSegment(sketch, "E70.right", {"start": v(-9.05, 40.36) * mm, "end": v(-9.05, 30.83) * mm});
            skLineSegment(sketch, "E71.bottom", {"start": v(0.58, 40.36) * mm, "end": v(-0.92, 40.36) * mm});
            skLineSegment(sketch, "E71.top", {"start": v(0.58, 30.71) * mm, "end": v(-0.92, 30.71) * mm});
            skLineSegment(sketch, "E71.left", {"start": v(0.58, 40.36) * mm, "end": v(0.58, 30.71) * mm});
            skLineSegment(sketch, "E71.right", {"start": v(-0.92, 40.36) * mm, "end": v(-0.92, 30.71) * mm});
            skLineSegment(sketch, "E72.bottom", {"start": v(3.69, 40.36) * mm, "end": v(5.18, 40.36) * mm});
            skLineSegment(sketch, "E72.top", {"start": v(3.69, 30.83) * mm, "end": v(5.18, 30.83) * mm});
            skLineSegment(sketch, "E72.left", {"start": v(3.69, 40.36) * mm, "end": v(3.69, 30.83) * mm});
            skLineSegment(sketch, "E72.right", {"start": v(5.18, 40.36) * mm, "end": v(5.18, 30.83) * mm});
            skLineSegment(sketch, "E73.bottom", {"start": v(12.99, 40.36) * mm, "end": v(14.48, 40.36) * mm});
            skLineSegment(sketch, "E73.top", {"start": v(12.99, 30.83) * mm, "end": v(14.48, 30.83) * mm});
            skLineSegment(sketch, "E73.left", {"start": v(12.99, 40.36) * mm, "end": v(12.99, 30.83) * mm});
            skLineSegment(sketch, "E73.right", {"start": v(14.48, 40.36) * mm, "end": v(14.48, 30.83) * mm});
            skLineSegment(sketch, "E74", {"start": v(-10.55, 38.52) * mm, "end": v(-9.05, 38.52) * mm});
            skLineSegment(sketch, "E75", {"start": v(-10.55, 35.6) * mm, "end": v(-9.05, 35.6) * mm});
            skLineSegment(sketch, "E76", {"start": v(-10.55, 33.13) * mm, "end": v(-9.05, 33.13) * mm});
            skLineSegment(sketch, "E77", {"start": v(-0.92, 38.3) * mm, "end": v(0.58, 38.3) * mm});
            skLineSegment(sketch, "E78", {"start": v(-0.92, 35.54) * mm, "end": v(0.58, 35.54) * mm});
            skLineSegment(sketch, "E79", {"start": v(-0.92, 33.13) * mm, "end": v(0.58, 33.13) * mm});
            skLineSegment(sketch, "E80", {"start": v(3.69, 38.3) * mm, "end": v(5.18, 38.3) * mm});
            skLineSegment(sketch, "E81", {"start": v(3.69, 35.6) * mm, "end": v(5.18, 35.6) * mm});
            skLineSegment(sketch, "E82", {"start": v(3.69, 32.9) * mm, "end": v(5.18, 32.9) * mm});
            skLineSegment(sketch, "E83", {"start": v(12.99, 33.13) * mm, "end": v(14.48, 33.13) * mm});
            skLineSegment(sketch, "E84", {"start": v(12.99, 35.6) * mm, "end": v(14.48, 35.6) * mm});
            skLineSegment(sketch, "E85", {"start": v(12.99, 38.4) * mm, "end": v(14.48, 38.4) * mm});
            skSolve(sketch);
        }
        {
            var Q0;
            Q0 = qSketchRegion(id + "F45", true);
            extrude(context, id + "F46", {"entities" : qUnion([Q0]), "operationType" : NewBodyOperationType.ADD, "depth" : 0.76 * mm, "offsetDistance" : 25.4 * mm});
        }
        {
            var Q0;
            Q0=makeQuery(id+"F40.opExtrude","SWEPT_FACE",FACE,{"disambiguationData":[OSD([sQuery(id+"F39.wireOp",EDGE,"E63.right")])]});
            var sketch = newSketch(context, id + "F47", { "sketchPlane" : qUnion([Q0])});
            skLineSegment(sketch, "E86.bottom", {"start": v(-7.68, 40.36) * mm, "end": v(-2.3, 40.36) * mm});
            skLineSegment(sketch, "E86.top", {"start": v(-7.68, 42.54) * mm, "end": v(-2.3, 42.54) * mm});
            skLineSegment(sketch, "E86.left", {"start": v(-7.68, 40.36) * mm, "end": v(-7.68, 42.54) * mm});
            skLineSegment(sketch, "E86.right", {"start": v(-2.3, 40.36) * mm, "end": v(-2.3, 42.54) * mm});
            skLineSegment(sketch, "E87.bottom", {"start": v(6.22, 40.36) * mm, "end": v(11.61, 40.36) * mm});
            skLineSegment(sketch, "E87.top", {"start": v(6.22, 42.54) * mm, "end": v(11.61, 42.54) * mm});
            skLineSegment(sketch, "E87.left", {"start": v(6.22, 40.36) * mm, "end": v(6.22, 42.54) * mm});
            skLineSegment(sketch, "E87.right", {"start": v(11.61, 40.36) * mm, "end": v(11.61, 42.54) * mm});
            skLineSegment(sketch, "E88.bottom", {"start": v(-7.68, 28.88) * mm, "end": v(-2.4, 28.88) * mm});
            skLineSegment(sketch, "E88.top", {"start": v(-7.68, 23.62) * mm, "end": v(-2.4, 23.62) * mm});
            skLineSegment(sketch, "E88.left", {"start": v(-7.68, 28.88) * mm, "end": v(-7.68, 23.62) * mm});
            skLineSegment(sketch, "E88.right", {"start": v(-2.4, 28.88) * mm, "end": v(-2.4, 23.62) * mm});
            skLineSegment(sketch, "E89.bottom", {"start": v(6.22, 29) * mm, "end": v(11.5, 29) * mm});
            skLineSegment(sketch, "E89.top", {"start": v(6.22, 23.62) * mm, "end": v(11.5, 23.62) * mm});
            skLineSegment(sketch, "E89.left", {"start": v(6.22, 29) * mm, "end": v(6.22, 23.62) * mm});
            skLineSegment(sketch, "E89.right", {"start": v(11.5, 29) * mm, "end": v(11.5, 23.62) * mm});
            skLineSegment(sketch, "E90.bottom", {"start": v(-22.37, 39.1) * mm, "end": v(-16.86, 39.1) * mm});
            skLineSegment(sketch, "E90.top", {"start": v(-22.37, 23.71) * mm, "end": v(-16.86, 23.71) * mm});
            skLineSegment(sketch, "E90.left", {"start": v(-22.37, 39.1) * mm, "end": v(-22.37, 23.71) * mm});
            skLineSegment(sketch, "E90.right", {"start": v(-16.86, 39.1) * mm, "end": v(-16.86, 23.71) * mm});
            skSolve(sketch);
        }
        {
            var Q0;
            Q0 = qSketchRegion(id + "F47", true);
            extrude(context, id + "F48", {"entities" : qUnion([Q0]), "operationType" : NewBodyOperationType.REMOVE, "oppositeDirection" : true, "depth" : 0.76 * mm, "offsetDistance" : 25.4 * mm});
        }
        {
            var Q0;
            Q0=makeQuery(id+"F42.boolean.opBoolean","COPY",FACE,{"derivedFrom":makeQuery(id+"F42.opExtrude","CAP_FACE",FACE,{"disambiguationData":[OSD([sQuery(id+"F41.wireOp",EDGE,"E67.bottom"),sQuery(id+"F41.wireOp",EDGE,"E67.top"),sQuery(id+"F41.wireOp",EDGE,"E67.left"),sQuery(id+"F41.wireOp",EDGE,"E67.right")])],"isStart":false})});
            var sketch = newSketch(context, id + "F49", { "sketchPlane" : qUnion([Q0])});
            skLineSegment(sketch, "E91.bottom", {"start": v(-21.92, 40.36) * mm, "end": v(-17.2, 40.36) * mm});
            skLineSegment(sketch, "E91.top", {"start": v(-21.92, 23.62) * mm, "end": v(-17.2, 23.62) * mm});
            skLineSegment(sketch, "E91.left", {"start": v(-21.92, 40.36) * mm, "end": v(-21.92, 23.62) * mm});
            skLineSegment(sketch, "E91.right", {"start": v(-17.2, 40.36) * mm, "end": v(-17.2, 23.62) * mm});
            skSolve(sketch);
        }
        {
            var Q0;
            Q0 = qSketchRegion(id + "F49", true);
            extrude(context, id + "F50", {"entities" : qUnion([Q0]), "operationType" : NewBodyOperationType.REMOVE, "oppositeDirection" : true, "depth" : 4.57 * mm, "offsetDistance" : 25.4 * mm});
        }
        {
            var Q0;
            Q0=makeQuery(id+"F40.opExtrude","CAP_FACE",FACE,{"disambiguationData":[OSD([sQuery(id+"F39.wireOp",EDGE,"E63.bottom"),sQuery(id+"F39.wireOp",EDGE,"E63.top"),sQuery(id+"F39.wireOp",EDGE,"E63.left"),sQuery(id+"F39.wireOp",EDGE,"E63.right"),sQuery(id+"F39.wireOp",EDGE,"E64.bottom"),sQuery(id+"F39.wireOp",EDGE,"E64.top"),sQuery(id+"F39.wireOp",EDGE,"E64.left"),sQuery(id+"F39.wireOp",EDGE,"E64.right"),sQuery(id+"F39.wireOp",EDGE,"E65.bottom"),sQuery(id+"F39.wireOp",EDGE,"E65.top"),sQuery(id+"F39.wireOp",EDGE,"E66.bottom"),sQuery(id+"F39.wireOp",EDGE,"E66.top")])],"isStart":false});
            var sketch = newSketch(context, id + "F51", { "sketchPlane" : qUnion([Q0])});
            skLineSegment(sketch, "E92.bottom", {"start": v(-16.03, 16.58) * mm, "end": v(7.43, 16.58) * mm});
            skLineSegment(sketch, "E92.top", {"start": v(-16.03, -39.23) * mm, "end": v(7.43, -39.23) * mm});
            skLineSegment(sketch, "E92.left", {"start": v(-16.03, 16.58) * mm, "end": v(-16.03, -39.23) * mm});
            skLineSegment(sketch, "E92.right", {"start": v(7.43, 16.58) * mm, "end": v(7.43, -39.23) * mm});
            skSolve(sketch);
        }
        {
            var Q0;
            Q0 = qSketchRegion(id + "F51", true);
            extrude(context, id + "F52", {"entities" : qUnion([Q0]), "operationType" : NewBodyOperationType.ADD, "depth" : 19.05 * mm, "offsetDistance" : 25.4 * mm});
        }
        {
            var Q0;
            Q0=makeQuery(id+"F52.boolean.opBoolean","MERGE",FACE,{"derivedFrom":[makeQuery(id+"F40.opExtrude","SWEPT_FACE",FACE,{"disambiguationData":[OSD([sQuery(id+"F39.wireOp",EDGE,"E63.right")])]}),makeQuery(id+"F52.opExtrude","SWEPT_FACE",FACE,{"disambiguationData":[OSD([sQuery(id+"F51.wireOp",EDGE,"E92.right")])]})]});
            var sketch = newSketch(context, id + "F53", { "sketchPlane" : qUnion([Q0])});
            skLineSegment(sketch, "E93.bottom", {"start": v(-39.23, 68.07) * mm, "end": v(16.58, 68.07) * mm});
            skLineSegment(sketch, "E93.top", {"start": v(-39.23, 49.02) * mm, "end": v(16.58, 49.02) * mm});
            skLineSegment(sketch, "E93.left", {"start": v(-39.23, 68.07) * mm, "end": v(-39.23, 49.02) * mm});
            skLineSegment(sketch, "E93.right", {"start": v(16.58, 68.07) * mm, "end": v(16.58, 49.02) * mm});
            skSolve(sketch);
        }
        {
            var Q0;
            Q0 = qSketchRegion(id + "F53", true);
            extrude(context, id + "F54", {"entities" : qUnion([Q0]), "operationType" : NewBodyOperationType.ADD, "depth" : 12.7 * mm, "offsetDistance" : 25.4 * mm});
        }
        {
            var Q0;
            Q0=makeQuery(id+"F52.boolean.opBoolean","MERGE",FACE,{"derivedFrom":[makeQuery(id+"F40.opExtrude","SWEPT_FACE",FACE,{"disambiguationData":[OSD([sQuery(id+"F39.wireOp",EDGE,"E64.left")])]}),makeQuery(id+"F52.opExtrude","SWEPT_FACE",FACE,{"disambiguationData":[OSD([sQuery(id+"F51.wireOp",EDGE,"E92.left")])]})]});
            var sketch = newSketch(context, id + "F55", { "sketchPlane" : qUnion([Q0])});
            skLineSegment(sketch, "E94.bottom", {"start": v(-16.58, 68.07) * mm, "end": v(39.23, 68.07) * mm});
            skLineSegment(sketch, "E94.top", {"start": v(-16.58, 49.02) * mm, "end": v(39.23, 49.02) * mm});
            skLineSegment(sketch, "E94.left", {"start": v(-16.58, 68.07) * mm, "end": v(-16.58, 49.02) * mm});
            skLineSegment(sketch, "E94.right", {"start": v(39.23, 68.07) * mm, "end": v(39.23, 49.02) * mm});
            skSolve(sketch);
        }
        {
            var Q0;
            Q0 = qSketchRegion(id + "F55", true);
            extrude(context, id + "F56", {"entities" : qUnion([Q0]), "operationType" : NewBodyOperationType.ADD, "depth" : 19.05 * mm, "offsetDistance" : 25.4 * mm});
        }
        {
            var Q0;
            Q0=makeQuery(id+"F54.opExtrude","CAP_FACE",FACE,{"disambiguationData":[OSD([sQuery(id+"F53.wireOp",EDGE,"E93.bottom"),sQuery(id+"F53.wireOp",EDGE,"E93.top"),sQuery(id+"F53.wireOp",EDGE,"E93.left"),sQuery(id+"F53.wireOp",EDGE,"E93.right")])],"isStart":false});
            var sketch = newSketch(context, id + "F57", { "sketchPlane" : qUnion([Q0])});
            skLineSegment(sketch, "E95.bottom", {"start": v(-45.4, 68.07) * mm, "end": v(23.26, 68.07) * mm});
            skLineSegment(sketch, "E95.top", {"start": v(-45.4, 70.5) * mm, "end": v(23.26, 70.5) * mm});
            skLineSegment(sketch, "E95.left", {"start": v(-45.4, 68.07) * mm, "end": v(-45.4, 70.5) * mm});
            skLineSegment(sketch, "E95.right", {"start": v(23.26, 68.07) * mm, "end": v(23.26, 70.5) * mm});
            skLineSegment(sketch, "E96", {"start": v(-45.4, 70.5) * mm, "end": v(-33.74, 85.27) * mm});
            skLineSegment(sketch, "E97", {"start": v(-33.74, 85.27) * mm, "end": v(11.59, 85.27) * mm});
            skLineSegment(sketch, "E98", {"start": v(11.59, 85.27) * mm, "end": v(23.26, 70.5) * mm});
            skSolve(sketch);
        }
        {
            var Q0;
            Q0 = qSketchRegion(id + "F57", true);
            extrude(context, id + "F58", {"entities" : qUnion([Q0]), "operationType" : NewBodyOperationType.ADD, "oppositeDirection" : true, "depth" : 57.15 * mm, "offsetDistance" : 25.4 * mm});
        }
        {
            var Q0;
            Q0=makeQuery(id+"F58.opExtrude","SWEPT_FACE",FACE,{"disambiguationData":[OSD([sQuery(id+"F57.wireOp",EDGE,"E97")])]});
            var sketch = newSketch(context, id + "F59", { "sketchPlane" : qUnion([Q0])});
            skLineSegment(sketch, "E99.bottom", {"start": v(-28.42, -3.78) * mm, "end": v(-17.9, -3.78) * mm});
            skLineSegment(sketch, "E99.top", {"start": v(-28.42, 7.4) * mm, "end": v(-17.9, 7.4) * mm});
            skLineSegment(sketch, "E99.left", {"start": v(-28.42, -3.78) * mm, "end": v(-28.42, 7.4) * mm});
            skLineSegment(sketch, "E99.right", {"start": v(-17.9, -3.78) * mm, "end": v(-17.9, 7.4) * mm});
            skSolve(sketch);
        }
        {
            var Q0;
            Q0 = qSketchRegion(id + "F59", true);
            extrude(context, id + "F60", {"entities" : qUnion([Q0]), "operationType" : NewBodyOperationType.ADD, "depth" : 19.05 * mm, "offsetDistance" : 25.4 * mm});
        }
        {
            var Q0;
            Q0=makeQuery(id+"F58.boolean.opBoolean","MERGE",FACE,{"derivedFrom":[makeQuery(id+"F54.opExtrude","CAP_FACE",FACE,{"disambiguationData":[OSD([sQuery(id+"F53.wireOp",EDGE,"E93.bottom"),sQuery(id+"F53.wireOp",EDGE,"E93.top"),sQuery(id+"F53.wireOp",EDGE,"E93.left"),sQuery(id+"F53.wireOp",EDGE,"E93.right")])],"isStart":false}),makeQuery(id+"F58.opExtrude","CAP_FACE",FACE,{"disambiguationData":[OSD([sQuery(id+"F57.wireOp",EDGE,"E95.bottom"),sQuery(id+"F57.wireOp",EDGE,"E95.left"),sQuery(id+"F57.wireOp",EDGE,"E95.right"),sQuery(id+"F57.wireOp",EDGE,"E96"),sQuery(id+"F57.wireOp",EDGE,"E97"),sQuery(id+"F57.wireOp",EDGE,"E98")])],"isStart":true})]});
            var sketch = newSketch(context, id + "F61", { "sketchPlane" : qUnion([Q0])});
            skLineSegment(sketch, "E100.bottom", {"start": v(-32.27, 68.07) * mm, "end": v(-19.88, 68.07) * mm});
            skLineSegment(sketch, "E100.top", {"start": v(-32.27, 53.94) * mm, "end": v(-19.88, 53.94) * mm});
            skLineSegment(sketch, "E100.left", {"start": v(-32.27, 68.07) * mm, "end": v(-32.27, 53.94) * mm});
            skLineSegment(sketch, "E100.right", {"start": v(-19.88, 68.07) * mm, "end": v(-19.88, 53.94) * mm});
            skLineSegment(sketch, "E101.bottom", {"start": v(-2.98, 68.07) * mm, "end": v(10.12, 68.07) * mm});
            skLineSegment(sketch, "E101.top", {"start": v(-2.98, 53.94) * mm, "end": v(10.12, 53.94) * mm});
            skLineSegment(sketch, "E101.left", {"start": v(-2.98, 68.07) * mm, "end": v(-2.98, 53.94) * mm});
            skLineSegment(sketch, "E101.right", {"start": v(10.12, 68.07) * mm, "end": v(10.12, 53.94) * mm});
            skLineSegment(sketch, "E102.bottom", {"start": v(-28.46, 53.94) * mm, "end": v(-26.07, 53.94) * mm});
            skLineSegment(sketch, "E102.top", {"start": v(-28.46, 68.07) * mm, "end": v(-26.07, 68.07) * mm});
            skLineSegment(sketch, "E102.left", {"start": v(-28.46, 53.94) * mm, "end": v(-28.46, 68.07) * mm});
            skLineSegment(sketch, "E102.right", {"start": v(-26.07, 53.94) * mm, "end": v(-26.07, 68.07) * mm});
            skLineSegment(sketch, "E103.bottom", {"start": v(3.57, 53.94) * mm, "end": v(5.6, 53.94) * mm});
            skLineSegment(sketch, "E103.top", {"start": v(3.57, 68.07) * mm, "end": v(5.6, 68.07) * mm});
            skLineSegment(sketch, "E103.left", {"start": v(3.57, 53.94) * mm, "end": v(3.57, 68.07) * mm});
            skLineSegment(sketch, "E103.right", {"start": v(5.6, 53.94) * mm, "end": v(5.6, 68.07) * mm});
            skLineSegment(sketch, "E104.bottom", {"start": v(-32.27, 63) * mm, "end": v(-19.88, 63) * mm});
            skLineSegment(sketch, "E104.top", {"start": v(-32.27, 61) * mm, "end": v(-19.88, 61) * mm});
            skLineSegment(sketch, "E104.left", {"start": v(-32.27, 63) * mm, "end": v(-32.27, 61) * mm});
            skLineSegment(sketch, "E104.right", {"start": v(-19.88, 63) * mm, "end": v(-19.88, 61) * mm});
            skLineSegment(sketch, "E105.bottom", {"start": v(-2.98, 63) * mm, "end": v(10.12, 63) * mm});
            skLineSegment(sketch, "E105.top", {"start": v(-2.98, 61) * mm, "end": v(10.12, 61) * mm});
            skLineSegment(sketch, "E105.left", {"start": v(-2.98, 63) * mm, "end": v(-2.98, 61) * mm});
            skLineSegment(sketch, "E105.right", {"start": v(10.12, 63) * mm, "end": v(10.12, 61) * mm});
            skSolve(sketch);
        }
        {
            var Q0;
            {var subQ0=sQuery(id+"F61.wireOp",EDGE,"E100.right");var subQ1=sQuery(id+"F61.wireOp",EDGE,"E100.bottom");var subQ2=makeQuery(id+"F61.imprint","INTERSECT",VERTEX,{"derivedFrom":[subQ1,subQ0]});Q0=makeQuery(id+"F61.imprint","IMPRINT",FACE,{"disambiguationData":[TD([[makeQuery(id+"F61.imprint","IMPRINT",EDGE,{"disambiguationData":[TD([[subQ2,1.0]])],"derivedFrom":subQ1}),-1.0]])]});}
            var Q1;
            {var subQ0=sQuery(id+"F61.wireOp",EDGE,"E100.left");var subQ1=sQuery(id+"F61.wireOp",EDGE,"E100.top");var subQ2=makeQuery(id+"F61.imprint","INTERSECT",VERTEX,{"derivedFrom":[subQ1,subQ0]});Q1=makeQuery(id+"F61.imprint","IMPRINT",FACE,{"disambiguationData":[TD([[makeQuery(id+"F61.imprint","IMPRINT",EDGE,{"disambiguationData":[TD([[subQ2,-1.0]])],"derivedFrom":subQ1}),1.0]])]});}
            var Q2;
            {var subQ0=sQuery(id+"F61.wireOp",EDGE,"E100.right");var subQ1=sQuery(id+"F61.wireOp",EDGE,"E100.top");var subQ2=makeQuery(id+"F61.imprint","INTERSECT",VERTEX,{"derivedFrom":[subQ1,subQ0]});Q2=makeQuery(id+"F61.imprint","IMPRINT",FACE,{"disambiguationData":[TD([[makeQuery(id+"F61.imprint","IMPRINT",EDGE,{"disambiguationData":[TD([[subQ2,1.0]])],"derivedFrom":subQ1}),1.0]])]});}
            var Q3;
            {var subQ0=sQuery(id+"F61.wireOp",EDGE,"E101.left");var subQ1=sQuery(id+"F61.wireOp",EDGE,"E101.bottom");var subQ2=makeQuery(id+"F61.imprint","INTERSECT",VERTEX,{"derivedFrom":[subQ1,subQ0]});Q3=makeQuery(id+"F61.imprint","IMPRINT",FACE,{"disambiguationData":[TD([[makeQuery(id+"F61.imprint","IMPRINT",EDGE,{"disambiguationData":[TD([[subQ2,-1.0]])],"derivedFrom":subQ1}),-1.0]])]});}
            var Q4;
            {var subQ0=sQuery(id+"F61.wireOp",EDGE,"E101.right");var subQ1=sQuery(id+"F61.wireOp",EDGE,"E101.bottom");var subQ2=makeQuery(id+"F61.imprint","INTERSECT",VERTEX,{"derivedFrom":[subQ1,subQ0]});Q4=makeQuery(id+"F61.imprint","IMPRINT",FACE,{"disambiguationData":[TD([[makeQuery(id+"F61.imprint","IMPRINT",EDGE,{"disambiguationData":[TD([[subQ2,1.0]])],"derivedFrom":subQ1}),-1.0]])]});}
            var Q5;
            {var subQ0=sQuery(id+"F61.wireOp",EDGE,"E101.left");var subQ1=sQuery(id+"F61.wireOp",EDGE,"E101.top");var subQ2=makeQuery(id+"F61.imprint","INTERSECT",VERTEX,{"derivedFrom":[subQ1,subQ0]});Q5=makeQuery(id+"F61.imprint","IMPRINT",FACE,{"disambiguationData":[TD([[makeQuery(id+"F61.imprint","IMPRINT",EDGE,{"disambiguationData":[TD([[subQ2,-1.0]])],"derivedFrom":subQ1}),1.0]])]});}
            var Q6;
            {var subQ0=sQuery(id+"F61.wireOp",EDGE,"E101.right");var subQ1=sQuery(id+"F61.wireOp",EDGE,"E101.top");var subQ2=makeQuery(id+"F61.imprint","INTERSECT",VERTEX,{"derivedFrom":[subQ1,subQ0]});Q6=makeQuery(id+"F61.imprint","IMPRINT",FACE,{"disambiguationData":[TD([[makeQuery(id+"F61.imprint","IMPRINT",EDGE,{"disambiguationData":[TD([[subQ2,1.0]])],"derivedFrom":subQ1}),1.0]])]});}
            var Q7;
            {var subQ0=sQuery(id+"F61.wireOp",EDGE,"E100.left");var subQ1=sQuery(id+"F61.wireOp",EDGE,"E100.bottom");var subQ2=makeQuery(id+"F61.imprint","INTERSECT",VERTEX,{"derivedFrom":[subQ1,subQ0]});Q7=makeQuery(id+"F61.imprint","IMPRINT",FACE,{"disambiguationData":[TD([[makeQuery(id+"F61.imprint","IMPRINT",EDGE,{"disambiguationData":[TD([[subQ2,-1.0]])],"derivedFrom":subQ1}),-1.0]])]});}
            extrude(context, id + "F62", {"entities" : qUnion([Q0, Q1, Q2, Q3, Q4, Q5, Q6, Q7]), "operationType" : NewBodyOperationType.REMOVE, "endBound" : BoundingType.THROUGH_ALL, "oppositeDirection" : true, "depth" : 25.4 * mm, "offsetDistance" : 25.4 * mm});
        }
        {
            var Q0;
            {var subQ0=sQuery(id+"F51.wireOp",EDGE,"E92.top");var subQ1=sQuery(id+"F51.wireOp",EDGE,"E92.right");var subQ2=sQuery(id+"F51.wireOp",EDGE,"E92.left");Q0=makeQuery(id+"F56.boolean.opBoolean","MERGE",FACE,{"derivedFrom":[makeQuery(id+"F54.boolean.opBoolean","MERGE",FACE,{"derivedFrom":[makeQuery(id+"F52.boolean.opBoolean","SPLIT",FACE,{"disambiguationData":[TD([makeQuery(id+"F40.opExtrude","SWEPT_FACE",FACE,{"disambiguationData":[OSD([sQuery(id+"F39.wireOp",EDGE,"E63.right")])]})])],"derivedFrom":makeQuery(id+"F52.opExtrude","CAP_FACE",FACE,{"disambiguationData":[OSD([sQuery(id+"F51.wireOp",EDGE,"E92.bottom"),subQ0,subQ2,subQ1])],"isStart":true})}),makeQuery(id+"F54.opExtrude","SWEPT_FACE",FACE,{"disambiguationData":[OSD([sQuery(id+"F53.wireOp",EDGE,"E93.top")])]})]}),makeQuery(id+"F56.opExtrude","SWEPT_FACE",FACE,{"disambiguationData":[OSD([sQuery(id+"F55.wireOp",EDGE,"E94.top")])]})]});}
            var sketch = newSketch(context, id + "F63", { "sketchPlane" : qUnion([Q0])});
            skLineSegment(sketch, "E106.bottom", {"start": v(-35.08, 39.23) * mm, "end": v(-28.81, 39.23) * mm});
            skLineSegment(sketch, "E106.top", {"start": v(-35.08, 29.17) * mm, "end": v(-28.81, 29.17) * mm});
            skLineSegment(sketch, "E106.left", {"start": v(-35.08, 39.23) * mm, "end": v(-35.08, 29.17) * mm});
            skLineSegment(sketch, "E106.right", {"start": v(-28.81, 39.23) * mm, "end": v(-28.81, 29.17) * mm});
            skSolve(sketch);
        }
        {
            var Q0;
            Q0 = qSketchRegion(id + "F63", true);
            extrude(context, id + "F64", {"entities" : qUnion([Q0]), "operationType" : NewBodyOperationType.ADD, "depth" : 57.15 * mm, "offsetDistance" : 25.4 * mm});
        }
        {
            var Q0;
            Q0=makeQuery(id+"F64.opExtrude","SWEPT_FACE",FACE,{"disambiguationData":[OSD([sQuery(id+"F63.wireOp",EDGE,"E106.top")])]});
            var sketch = newSketch(context, id + "F65", { "sketchPlane" : qUnion([Q0])});
            skLineSegment(sketch, "E107.bottom", {"start": v(28.81, 45.6) * mm, "end": v(35.08, 45.6) * mm});
            skLineSegment(sketch, "E107.top", {"start": v(28.81, 44.18) * mm, "end": v(35.08, 44.18) * mm});
            skLineSegment(sketch, "E107.left", {"start": v(28.81, 45.6) * mm, "end": v(28.81, 44.18) * mm});
            skLineSegment(sketch, "E107.right", {"start": v(35.08, 45.6) * mm, "end": v(35.08, 44.18) * mm});
            skLineSegment(sketch, "E108.bottom", {"start": v(28.81, 38.47) * mm, "end": v(35.08, 38.47) * mm});
            skLineSegment(sketch, "E108.top", {"start": v(28.81, 36.8) * mm, "end": v(35.08, 36.8) * mm});
            skLineSegment(sketch, "E108.left", {"start": v(28.81, 38.47) * mm, "end": v(28.81, 36.8) * mm});
            skLineSegment(sketch, "E108.right", {"start": v(35.08, 38.47) * mm, "end": v(35.08, 36.8) * mm});
            skSolve(sketch);
        }
        {
            var Q0;
            Q0 = qSketchRegion(id + "F65", true);
            extrude(context, id + "F66", {"entities" : qUnion([Q0]), "operationType" : NewBodyOperationType.ADD, "depth" : 44.45 * mm, "offsetDistance" : 25.4 * mm});
        }
        {
            var Q0;
            Q0=makeQuery(id+"F66.opExtrude","SWEPT_FACE",FACE,{"disambiguationData":[OSD([sQuery(id+"F65.wireOp",EDGE,"E108.top")])]});
            var sketch = newSketch(context, id + "F67", { "sketchPlane" : qUnion([Q0])});
            skLineSegment(sketch, "E109.bottom", {"start": v(-35.08, -15.28) * mm, "end": v(-28.81, -15.28) * mm});
            skLineSegment(sketch, "E109.top", {"start": v(-35.08, -9.29) * mm, "end": v(-28.81, -9.29) * mm});
            skLineSegment(sketch, "E109.left", {"start": v(-35.08, -15.28) * mm, "end": v(-35.08, -9.29) * mm});
            skLineSegment(sketch, "E109.right", {"start": v(-28.81, -15.28) * mm, "end": v(-28.81, -9.29) * mm});
            skSolve(sketch);
        }
        {
            var Q0;
            Q0 = qSketchRegion(id + "F67", true);
            extrude(context, id + "F68", {"entities" : qUnion([Q0]), "operationType" : NewBodyOperationType.ADD, "depth" : 44.45 * mm, "offsetDistance" : 25.4 * mm});
        }
        {
            var Q0;
            Q0=makeQuery(id+"F64.boolean.opBoolean","MERGE",FACE,{"derivedFrom":[makeQuery(id+"F56.boolean.opBoolean","MERGE",FACE,{"derivedFrom":[makeQuery(id+"F54.boolean.opBoolean","MERGE",FACE,{"derivedFrom":[makeQuery(id+"F52.opExtrude","SWEPT_FACE",FACE,{"disambiguationData":[OSD([sQuery(id+"F51.wireOp",EDGE,"E92.top")])]}),makeQuery(id+"F54.opExtrude","SWEPT_FACE",FACE,{"disambiguationData":[OSD([sQuery(id+"F53.wireOp",EDGE,"E93.left")])]})]}),makeQuery(id+"F56.opExtrude","SWEPT_FACE",FACE,{"disambiguationData":[OSD([sQuery(id+"F55.wireOp",EDGE,"E94.right")])]})]}),makeQuery(id+"F64.opExtrude","SWEPT_FACE",FACE,{"disambiguationData":[OSD([sQuery(id+"F63.wireOp",EDGE,"E106.bottom")])]})]});
            var sketch = newSketch(context, id + "F69", { "sketchPlane" : qUnion([Q0])});
            skLineSegment(sketch, "E110.bottom", {"start": v(-28.81, 65.37) * mm, "end": v(16.9, 65.37) * mm});
            skLineSegment(sketch, "E110.top", {"start": v(-28.81, 59.42) * mm, "end": v(16.9, 59.42) * mm});
            skLineSegment(sketch, "E110.left", {"start": v(-28.81, 65.37) * mm, "end": v(-28.81, 59.42) * mm});
            skLineSegment(sketch, "E110.right", {"start": v(16.9, 65.37) * mm, "end": v(16.9, 59.42) * mm});
            skLineSegment(sketch, "E111.bottom", {"start": v(-23.1, 65.37) * mm, "end": v(-21.43, 65.37) * mm});
            skLineSegment(sketch, "E111.top", {"start": v(-23.1, 59.42) * mm, "end": v(-21.43, 59.42) * mm});
            skLineSegment(sketch, "E111.left", {"start": v(-23.1, 65.37) * mm, "end": v(-23.1, 59.42) * mm});
            skLineSegment(sketch, "E111.right", {"start": v(-21.43, 65.37) * mm, "end": v(-21.43, 59.42) * mm});
            skLineSegment(sketch, "E112.bottom", {"start": v(-16.67, 65.37) * mm, "end": v(-15.24, 65.37) * mm});
            skLineSegment(sketch, "E112.top", {"start": v(-16.67, 59.42) * mm, "end": v(-15.24, 59.42) * mm});
            skLineSegment(sketch, "E112.left", {"start": v(-16.67, 65.37) * mm, "end": v(-16.67, 59.42) * mm});
            skLineSegment(sketch, "E112.right", {"start": v(-15.24, 65.37) * mm, "end": v(-15.24, 59.42) * mm});
            skLineSegment(sketch, "E113.bottom", {"start": v(12.38, 65.37) * mm, "end": v(10.24, 65.37) * mm});
            skLineSegment(sketch, "E113.top", {"start": v(12.38, 59.42) * mm, "end": v(10.24, 59.42) * mm});
            skLineSegment(sketch, "E113.left", {"start": v(12.38, 65.37) * mm, "end": v(12.38, 59.42) * mm});
            skLineSegment(sketch, "E113.right", {"start": v(10.24, 65.37) * mm, "end": v(10.24, 59.42) * mm});
            skLineSegment(sketch, "E114.bottom", {"start": v(5.48, 65.37) * mm, "end": v(3.57, 65.37) * mm});
            skLineSegment(sketch, "E114.top", {"start": v(5.48, 59.42) * mm, "end": v(3.57, 59.42) * mm});
            skLineSegment(sketch, "E114.left", {"start": v(5.48, 65.37) * mm, "end": v(5.48, 59.42) * mm});
            skLineSegment(sketch, "E114.right", {"start": v(3.57, 65.37) * mm, "end": v(3.57, 59.42) * mm});
            skLineSegment(sketch, "E115.bottom", {"start": v(-10.48, 65.37) * mm, "end": v(-8.57, 65.37) * mm});
            skLineSegment(sketch, "E115.top", {"start": v(-10.48, 59.42) * mm, "end": v(-8.57, 59.42) * mm});
            skLineSegment(sketch, "E115.left", {"start": v(-10.48, 65.37) * mm, "end": v(-10.48, 59.42) * mm});
            skLineSegment(sketch, "E115.right", {"start": v(-8.57, 65.37) * mm, "end": v(-8.57, 59.42) * mm});
            skLineSegment(sketch, "E116.bottom", {"start": v(-4.05, 65.37) * mm, "end": v(-2.62, 65.37) * mm});
            skLineSegment(sketch, "E116.top", {"start": v(-4.05, 59.42) * mm, "end": v(-2.62, 59.42) * mm});
            skLineSegment(sketch, "E116.left", {"start": v(-4.05, 65.37) * mm, "end": v(-4.05, 59.42) * mm});
            skLineSegment(sketch, "E116.right", {"start": v(-2.62, 65.37) * mm, "end": v(-2.62, 59.42) * mm});
            skSolve(sketch);
        }
        {
            var Q0;
            {var subQ0=sQuery(id+"F69.wireOp",EDGE,"E110.right");Q0=makeQuery(id+"F69.imprint","IMPRINT",FACE,{"disambiguationData":[TD([[makeQuery(id+"F69.imprint","IMPRINT",EDGE,{"derivedFrom":subQ0}),-1.0]])]});}
            var Q1;
            {var subQ0=sQuery(id+"F69.wireOp",EDGE,"E111.right");Q1=makeQuery(id+"F69.imprint","IMPRINT",FACE,{"disambiguationData":[TD([[makeQuery(id+"F69.imprint","IMPRINT",EDGE,{"derivedFrom":subQ0}),1.0]])]});}
            var Q2;
            {var subQ0=sQuery(id+"F69.wireOp",EDGE,"E112.right");Q2=makeQuery(id+"F69.imprint","IMPRINT",FACE,{"disambiguationData":[TD([[makeQuery(id+"F69.imprint","IMPRINT",EDGE,{"derivedFrom":subQ0}),1.0]])]});}
            var Q3;
            {var subQ0=sQuery(id+"F69.wireOp",EDGE,"E115.right");Q3=makeQuery(id+"F69.imprint","IMPRINT",FACE,{"disambiguationData":[TD([[makeQuery(id+"F69.imprint","IMPRINT",EDGE,{"derivedFrom":subQ0}),1.0]])]});}
            var Q4;
            {var subQ0=sQuery(id+"F69.wireOp",EDGE,"E114.right");Q4=makeQuery(id+"F69.imprint","IMPRINT",FACE,{"disambiguationData":[TD([[makeQuery(id+"F69.imprint","IMPRINT",EDGE,{"derivedFrom":subQ0}),-1.0]])]});}
            var Q5;
            {var subQ0=sQuery(id+"F69.wireOp",EDGE,"E113.right");Q5=makeQuery(id+"F69.imprint","IMPRINT",FACE,{"disambiguationData":[TD([[makeQuery(id+"F69.imprint","IMPRINT",EDGE,{"derivedFrom":subQ0}),-1.0]])]});}
            var Q6;
            {var subQ0=sQuery(id+"F69.wireOp",EDGE,"E110.left");Q6=makeQuery(id+"F69.imprint","IMPRINT",FACE,{"disambiguationData":[TD([[makeQuery(id+"F69.imprint","IMPRINT",EDGE,{"derivedFrom":subQ0}),1.0]])]});}
            extrude(context, id + "F70", {"entities" : qUnion([Q0, Q1, Q2, Q3, Q4, Q5, Q6]), "operationType" : NewBodyOperationType.REMOVE, "oppositeDirection" : true, "depth" : 2.03 * mm, "offsetDistance" : 25.4 * mm});
        }
        {
            var Q0;
            Q0=makeQuery(id+"F40.opExtrude","SWEPT_FACE",FACE,{"disambiguationData":[OSD([sQuery(id+"F39.wireOp",EDGE,"E63.bottom"),sQuery(id+"F39.wireOp",EDGE,"E64.bottom"),sQuery(id+"F39.wireOp",EDGE,"E65.bottom")])]});
            var sketch = newSketch(context, id + "F71", { "sketchPlane" : qUnion([Q0])});
            skLineSegment(sketch, "E117.bottom", {"start": v(-9.76, 45.13) * mm, "end": v(2.38, 45.13) * mm});
            skLineSegment(sketch, "E117.top", {"start": v(-9.76, 28.23) * mm, "end": v(2.38, 28.23) * mm});
            skLineSegment(sketch, "E117.left", {"start": v(-9.76, 45.13) * mm, "end": v(-9.76, 28.23) * mm});
            skLineSegment(sketch, "E117.right", {"start": v(2.38, 45.13) * mm, "end": v(2.38, 28.23) * mm});
            skSolve(sketch);
        }
        {
            var Q0;
            Q0 = qSketchRegion(id + "F71", true);
            extrude(context, id + "F72", {"entities" : qUnion([Q0]), "operationType" : NewBodyOperationType.REMOVE, "oppositeDirection" : true, "depth" : 6.35 * mm, "offsetDistance" : 25.4 * mm});
        }
        {
            var Q0;
            Q0=makeQuery(id+"F40.opExtrude","SWEPT_FACE",FACE,{"disambiguationData":[OSD([sQuery(id+"F39.wireOp",EDGE,"E63.bottom"),sQuery(id+"F39.wireOp",EDGE,"E64.bottom"),sQuery(id+"F39.wireOp",EDGE,"E65.bottom")])]});
            var sketch = newSketch(context, id + "F73", { "sketchPlane" : qUnion([Q0])});
            skLineSegment(sketch, "E118.bottom", {"start": v(-9.76, 28.23) * mm, "end": v(2.38, 28.23) * mm});
            skLineSegment(sketch, "E118.top", {"start": v(-9.76, 26.08) * mm, "end": v(2.38, 26.08) * mm});
            skLineSegment(sketch, "E118.left", {"start": v(-9.76, 28.23) * mm, "end": v(-9.76, 26.08) * mm});
            skLineSegment(sketch, "E118.right", {"start": v(2.38, 28.23) * mm, "end": v(2.38, 26.08) * mm});
            skLineSegment(sketch, "E119.bottom", {"start": v(-9.76, 45.13) * mm, "end": v(2.38, 45.13) * mm});
            skLineSegment(sketch, "E119.top", {"start": v(-9.76, 47.28) * mm, "end": v(2.38, 47.28) * mm});
            skLineSegment(sketch, "E119.left", {"start": v(-9.76, 45.13) * mm, "end": v(-9.76, 47.28) * mm});
            skLineSegment(sketch, "E119.right", {"start": v(2.38, 45.13) * mm, "end": v(2.38, 47.28) * mm});
            skSolve(sketch);
        }
        {
            var Q0;
            Q0 = qSketchRegion(id + "F73", true);
            extrude(context, id + "F74", {"entities" : qUnion([Q0]), "operationType" : NewBodyOperationType.REMOVE, "oppositeDirection" : true, "depth" : 1.78 * mm, "offsetDistance" : 25.4 * mm});
        }
        {
            var Q0;
            {var subQ2=sQuery(id+"F10.wireOp",EDGE,"E18.bottom");var subQ3=sQuery(id+"F0.wireOp",EDGE,"E0.right");var subQ4=sQuery(id+"F0.wireOp",EDGE,"E0.bottom");var subQ10=sQuery(id+"F10.wireOp",EDGE,"E19.bottom");var subQ11=sQuery(id+"F17.wireOp",EDGE,"E34.bottom");var subQ12=sQuery(id+"F17.wireOp",EDGE,"E33.bottom");var subQ14=sQuery(id+"F17.wireOp",EDGE,"E32.bottom");var subQ18=sQuery(id+"F25.wireOp",EDGE,"E44.bottom");var subQ19=makeQuery(id+"F26.boolean.opBoolean","MERGE",FACE,{"derivedFrom":[makeQuery(id+"F18.boolean.opBoolean","MERGE",FACE,{"derivedFrom":[makeQuery(id+"F11.boolean.opBoolean","MERGE",FACE,{"derivedFrom":[makeQuery(id+"F1.opExtrude","SWEPT_FACE",FACE,{"disambiguationData":[OSD([subQ4])]}),makeQuery(id+"F11.opExtrude","SWEPT_FACE",FACE,{"disambiguationData":[OSD([subQ2])]}),makeQuery(id+"F11.opExtrude","SWEPT_FACE",FACE,{"disambiguationData":[OSD([subQ10])]})]}),makeQuery(id+"F18.opExtrude","SWEPT_FACE",FACE,{"disambiguationData":[OSD([subQ14,subQ12,subQ11])]})]}),makeQuery(id+"F26.opExtrude","SWEPT_FACE",FACE,{"disambiguationData":[OSD([subQ18])]})]});Q0=makeQuery(id+"F50.boolean.opBoolean","MERGE",FACE,{"derivedFrom":[makeQuery(id+"F40.boolean.opBoolean","SPLIT",FACE,{"disambiguationData":[TD([makeQuery(id+"F40.opExtrude","SWEPT_FACE",FACE,{"disambiguationData":[OSD([sQuery(id+"F39.wireOp",EDGE,"E63.left")])]})])],"derivedFrom":subQ19}),makeQuery(id+"F48.boolean.opBoolean","MERGE",FACE,{"derivedFrom":[makeQuery(id+"F42.boolean.opBoolean","MERGE",FACE,{"derivedFrom":[makeQuery(id+"F40.boolean.opBoolean","SPLIT",FACE,{"disambiguationData":[TD([makeQuery(id+"F1.opExtrude","SWEPT_FACE",FACE,{"disambiguationData":[OSD([subQ3])]})])],"derivedFrom":subQ19}),makeQuery(id+"F42.opExtrude","SWEPT_FACE",FACE,{"disambiguationData":[OSD([sQuery(id+"F41.wireOp",EDGE,"E67.bottom")])]})]}),makeQuery(id+"F48.opExtrude","SWEPT_FACE",FACE,{"disambiguationData":[OSD([sQuery(id+"F47.wireOp",EDGE,"E88.top")])]}),makeQuery(id+"F48.opExtrude","SWEPT_FACE",FACE,{"disambiguationData":[OSD([sQuery(id+"F47.wireOp",EDGE,"E89.top")])]})]}),makeQuery(id+"F50.opExtrude","SWEPT_FACE",FACE,{"disambiguationData":[OSD([sQuery(id+"F49.wireOp",EDGE,"E91.top")])]})]});}
            var sketch = newSketch(context, id + "F75", { "sketchPlane" : qUnion([Q0])});
            skLineSegment(sketch, "E120", {"start": v(46.1, -18.43) * mm, "end": v(46.1, -29.9) * mm});
            skLineSegment(sketch, "E121", {"start": v(46.1, -29.9) * mm, "end": v(12.09, -29.9) * mm});
            skLineSegment(sketch, "E122", {"start": v(12.09, -29.9) * mm, "end": v(12.09, -22.14) * mm});
            skLineSegment(sketch, "E123", {"start": v(12.09, -22.14) * mm, "end": v(7.43, -23.52) * mm});
            skLineSegment(sketch, "E124", {"start": v(7.43, -23.52) * mm, "end": v(6.16, -21.92) * mm});
            skLineSegment(sketch, "E125", {"start": v(6.16, -21.92) * mm, "end": v(6.16, -17.2) * mm});
            skLineSegment(sketch, "E126", {"start": v(6.16, -17.2) * mm, "end": v(7.43, -15.6) * mm});
            skLineSegment(sketch, "E127", {"start": v(7.43, -15.6) * mm, "end": v(12.42, -15.6) * mm});
            skLineSegment(sketch, "E128", {"start": v(12.42, -15.6) * mm, "end": v(20.17, -15.6) * mm});
            skLineSegment(sketch, "E129", {"start": v(20.17, -15.6) * mm, "end": v(20.17, -21.92) * mm});
            skLineSegment(sketch, "E130", {"start": v(20.17, -21.92) * mm, "end": v(28.25, -21.92) * mm});
            skLineSegment(sketch, "E131", {"start": v(28.25, -21.92) * mm, "end": v(28.25, -18.43) * mm});
            skSolve(sketch);
        }
        {
            var Q0;
            Q0 = qSketchRegion(id + "F75", true);
            var Q1;
            {var subQ0=sQuery(id+"F75.wireOp",EDGE,"E120");Q1=makeQuery(id+"F75.imprint","IMPRINT",FACE,{"disambiguationData":[TD([[makeQuery(id+"F75.imprint","IMPRINT",EDGE,{"derivedFrom":subQ0}),-1.0]])]});}
            extrude(context, id + "F76", {"entities" : qUnion([Q0, Q1]), "operationType" : NewBodyOperationType.REMOVE, "oppositeDirection" : true, "depth" : 0.76 * mm, "offsetDistance" : 25.4 * mm});
        }
        {
            var Q0;
            Q0=makeQuery(id+"F56.boolean.opBoolean","MERGE",FACE,{"derivedFrom":[makeQuery(id+"F54.boolean.opBoolean","MERGE",FACE,{"derivedFrom":[makeQuery(id+"F52.boolean.opBoolean","MERGE",FACE,{"derivedFrom":[makeQuery(id+"F40.opExtrude","SWEPT_FACE",FACE,{"disambiguationData":[OSD([sQuery(id+"F39.wireOp",EDGE,"E63.top"),sQuery(id+"F39.wireOp",EDGE,"E64.top"),sQuery(id+"F39.wireOp",EDGE,"E66.bottom")])]}),makeQuery(id+"F52.opExtrude","SWEPT_FACE",FACE,{"disambiguationData":[OSD([sQuery(id+"F51.wireOp",EDGE,"E92.bottom")])]})]}),makeQuery(id+"F54.opExtrude","SWEPT_FACE",FACE,{"disambiguationData":[OSD([sQuery(id+"F53.wireOp",EDGE,"E93.right")])]})]}),makeQuery(id+"F56.opExtrude","SWEPT_FACE",FACE,{"disambiguationData":[OSD([sQuery(id+"F55.wireOp",EDGE,"E94.left")])]})]});
            var sketch = newSketch(context, id + "F77", { "sketchPlane" : qUnion([Q0])});
            skLineSegment(sketch, "E132.bottom", {"start": v(-2.26, 46.8) * mm, "end": v(10.12, 46.8) * mm});
            skLineSegment(sketch, "E132.top", {"start": v(-2.26, 28.47) * mm, "end": v(10.12, 28.47) * mm});
            skLineSegment(sketch, "E132.left", {"start": v(-2.26, 46.8) * mm, "end": v(-2.26, 28.47) * mm});
            skLineSegment(sketch, "E132.right", {"start": v(10.12, 46.8) * mm, "end": v(10.12, 28.47) * mm});
            skSolve(sketch);
        }
        {
            var Q0;
            Q0 = qSketchRegion(id + "F77", true);
            extrude(context, id + "F78", {"entities" : qUnion([Q0]), "operationType" : NewBodyOperationType.REMOVE, "oppositeDirection" : true, "depth" : 25.4 * mm, "offsetDistance" : 25.4 * mm});
        }
        {
            var Q0;
            Q0=makeQuery(id+"F56.boolean.opBoolean","MERGE",FACE,{"derivedFrom":[makeQuery(id+"F54.boolean.opBoolean","MERGE",FACE,{"derivedFrom":[makeQuery(id+"F52.boolean.opBoolean","MERGE",FACE,{"derivedFrom":[makeQuery(id+"F40.opExtrude","SWEPT_FACE",FACE,{"disambiguationData":[OSD([sQuery(id+"F39.wireOp",EDGE,"E63.top"),sQuery(id+"F39.wireOp",EDGE,"E64.top"),sQuery(id+"F39.wireOp",EDGE,"E66.bottom")])]}),makeQuery(id+"F52.opExtrude","SWEPT_FACE",FACE,{"disambiguationData":[OSD([sQuery(id+"F51.wireOp",EDGE,"E92.bottom")])]})]}),makeQuery(id+"F54.opExtrude","SWEPT_FACE",FACE,{"disambiguationData":[OSD([sQuery(id+"F53.wireOp",EDGE,"E93.right")])]})]}),makeQuery(id+"F56.opExtrude","SWEPT_FACE",FACE,{"disambiguationData":[OSD([sQuery(id+"F55.wireOp",EDGE,"E94.left")])]})]});
            var sketch = newSketch(context, id + "F79", { "sketchPlane" : qUnion([Q0])});
            skLineSegment(sketch, "E133.bottom", {"start": v(-2.26, 28.47) * mm, "end": v(10.12, 28.47) * mm});
            skLineSegment(sketch, "E133.top", {"start": v(-2.26, 26.56) * mm, "end": v(10.12, 26.56) * mm});
            skLineSegment(sketch, "E133.left", {"start": v(-2.26, 28.47) * mm, "end": v(-2.26, 26.56) * mm});
            skLineSegment(sketch, "E133.right", {"start": v(10.12, 28.47) * mm, "end": v(10.12, 26.56) * mm});
            skSolve(sketch);
        }
        {
            var Q0;
            Q0 = qSketchRegion(id + "F79", true);
            extrude(context, id + "F80", {"entities" : qUnion([Q0]), "operationType" : NewBodyOperationType.REMOVE, "oppositeDirection" : true, "depth" : 0.76 * mm, "offsetDistance" : 25.4 * mm});
        }
        {
            var Q0;
            Q0=makeQuery(id+"F56.boolean.opBoolean","MERGE",FACE,{"derivedFrom":[makeQuery(id+"F54.boolean.opBoolean","MERGE",FACE,{"derivedFrom":[makeQuery(id+"F52.boolean.opBoolean","MERGE",FACE,{"derivedFrom":[makeQuery(id+"F40.opExtrude","SWEPT_FACE",FACE,{"disambiguationData":[OSD([sQuery(id+"F39.wireOp",EDGE,"E63.top"),sQuery(id+"F39.wireOp",EDGE,"E64.top"),sQuery(id+"F39.wireOp",EDGE,"E66.bottom")])]}),makeQuery(id+"F52.opExtrude","SWEPT_FACE",FACE,{"disambiguationData":[OSD([sQuery(id+"F51.wireOp",EDGE,"E92.bottom")])]})]}),makeQuery(id+"F54.opExtrude","SWEPT_FACE",FACE,{"disambiguationData":[OSD([sQuery(id+"F53.wireOp",EDGE,"E93.right")])]})]}),makeQuery(id+"F56.opExtrude","SWEPT_FACE",FACE,{"disambiguationData":[OSD([sQuery(id+"F55.wireOp",EDGE,"E94.left")])]})]});
            var sketch = newSketch(context, id + "F81", { "sketchPlane" : qUnion([Q0])});
            skLineSegment(sketch, "E134.bottom", {"start": v(-13.7, 64.42) * mm, "end": v(-5.83, 64.42) * mm});
            skLineSegment(sketch, "E134.top", {"start": v(-13.7, 59.18) * mm, "end": v(-5.83, 59.18) * mm});
            skLineSegment(sketch, "E134.left", {"start": v(-13.7, 64.42) * mm, "end": v(-13.7, 59.18) * mm});
            skLineSegment(sketch, "E134.right", {"start": v(-5.83, 64.42) * mm, "end": v(-5.83, 59.18) * mm});
            skLineSegment(sketch, "E135.bottom", {"start": v(30.6, 64.42) * mm, "end": v(22.26, 64.42) * mm});
            skLineSegment(sketch, "E135.top", {"start": v(30.6, 59.18) * mm, "end": v(22.26, 59.18) * mm});
            skLineSegment(sketch, "E135.left", {"start": v(30.6, 64.42) * mm, "end": v(30.6, 59.18) * mm});
            skLineSegment(sketch, "E135.right", {"start": v(22.26, 64.42) * mm, "end": v(22.26, 59.18) * mm});
            skLineSegment(sketch, "E136.bottom", {"start": v(4.17, 64.18) * mm, "end": v(11.55, 64.18) * mm});
            skLineSegment(sketch, "E136.top", {"start": v(4.17, 55.37) * mm, "end": v(11.55, 55.37) * mm});
            skLineSegment(sketch, "E136.left", {"start": v(4.17, 64.18) * mm, "end": v(4.17, 55.37) * mm});
            skLineSegment(sketch, "E136.right", {"start": v(11.55, 64.18) * mm, "end": v(11.55, 55.37) * mm});
            skSolve(sketch);
        }
        {
            var Q0;
            Q0 = qSketchRegion(id + "F81", true);
            extrude(context, id + "F82", {"entities" : qUnion([Q0]), "operationType" : NewBodyOperationType.REMOVE, "oppositeDirection" : true, "depth" : 25.4 * mm, "offsetDistance" : 25.4 * mm});
        }
        {
            var Q0;
            Q0=makeQuery(id+"F56.boolean.opBoolean","MERGE",FACE,{"derivedFrom":[makeQuery(id+"F54.boolean.opBoolean","MERGE",FACE,{"derivedFrom":[makeQuery(id+"F52.boolean.opBoolean","MERGE",FACE,{"derivedFrom":[makeQuery(id+"F40.opExtrude","SWEPT_FACE",FACE,{"disambiguationData":[OSD([sQuery(id+"F39.wireOp",EDGE,"E63.top"),sQuery(id+"F39.wireOp",EDGE,"E64.top"),sQuery(id+"F39.wireOp",EDGE,"E66.bottom")])]}),makeQuery(id+"F52.opExtrude","SWEPT_FACE",FACE,{"disambiguationData":[OSD([sQuery(id+"F51.wireOp",EDGE,"E92.bottom")])]})]}),makeQuery(id+"F54.opExtrude","SWEPT_FACE",FACE,{"disambiguationData":[OSD([sQuery(id+"F53.wireOp",EDGE,"E93.right")])]})]}),makeQuery(id+"F56.opExtrude","SWEPT_FACE",FACE,{"disambiguationData":[OSD([sQuery(id+"F55.wireOp",EDGE,"E94.left")])]})]});
            var sketch = newSketch(context, id + "F83", { "sketchPlane" : qUnion([Q0])});
            skLineSegment(sketch, "E137.bottom", {"start": v(-13.7, 59.18) * mm, "end": v(-5.83, 59.18) * mm});
            skLineSegment(sketch, "E137.top", {"start": v(-13.7, 56.8) * mm, "end": v(-5.83, 56.8) * mm});
            skLineSegment(sketch, "E137.left", {"start": v(-13.7, 59.18) * mm, "end": v(-13.7, 56.8) * mm});
            skLineSegment(sketch, "E137.right", {"start": v(-5.83, 59.18) * mm, "end": v(-5.83, 56.8) * mm});
            skLineSegment(sketch, "E138.bottom", {"start": v(4.17, 55.37) * mm, "end": v(11.55, 55.37) * mm});
            skLineSegment(sketch, "E138.top", {"start": v(4.17, 53.23) * mm, "end": v(11.55, 53.23) * mm});
            skLineSegment(sketch, "E138.left", {"start": v(4.17, 55.37) * mm, "end": v(4.17, 53.23) * mm});
            skLineSegment(sketch, "E138.right", {"start": v(11.55, 55.37) * mm, "end": v(11.55, 53.23) * mm});
            skLineSegment(sketch, "E139.bottom", {"start": v(22.26, 59.18) * mm, "end": v(30.6, 59.18) * mm});
            skLineSegment(sketch, "E139.top", {"start": v(22.26, 55.37) * mm, "end": v(30.6, 55.37) * mm});
            skLineSegment(sketch, "E139.left", {"start": v(22.26, 59.18) * mm, "end": v(22.26, 55.37) * mm});
            skLineSegment(sketch, "E139.right", {"start": v(30.6, 59.18) * mm, "end": v(30.6, 55.37) * mm});
            skSolve(sketch);
        }
        {
            var Q0;
            Q0 = qSketchRegion(id + "F83", true);
            extrude(context, id + "F84", {"entities" : qUnion([Q0]), "operationType" : NewBodyOperationType.REMOVE, "oppositeDirection" : true, "depth" : 0.76 * mm, "offsetDistance" : 25.4 * mm});
        }
        {
            var Q0;
            Q0=makeQuery(id+"F68.boolean.opBoolean","MERGE",FACE,{"derivedFrom":[makeQuery(id+"F66.boolean.opBoolean","MERGE",FACE,{"derivedFrom":[makeQuery(id+"F64.boolean.opBoolean","MERGE",FACE,{"derivedFrom":[makeQuery(id+"F56.opExtrude","CAP_FACE",FACE,{"disambiguationData":[OSD([sQuery(id+"F55.wireOp",EDGE,"E94.bottom"),sQuery(id+"F55.wireOp",EDGE,"E94.top"),sQuery(id+"F55.wireOp",EDGE,"E94.left"),sQuery(id+"F55.wireOp",EDGE,"E94.right")])],"isStart":false}),makeQuery(id+"F64.opExtrude","SWEPT_FACE",FACE,{"disambiguationData":[OSD([sQuery(id+"F63.wireOp",EDGE,"E106.left")])]})]}),makeQuery(id+"F66.opExtrude","SWEPT_FACE",FACE,{"disambiguationData":[OSD([sQuery(id+"F65.wireOp",EDGE,"E107.right")])]}),makeQuery(id+"F66.opExtrude","SWEPT_FACE",FACE,{"disambiguationData":[OSD([sQuery(id+"F65.wireOp",EDGE,"E108.right")])]})]}),makeQuery(id+"F68.opExtrude","SWEPT_FACE",FACE,{"disambiguationData":[OSD([sQuery(id+"F67.wireOp",EDGE,"E109.left")])]})]});
            var sketch = newSketch(context, id + "F85", { "sketchPlane" : qUnion([Q0])});
            skLineSegment(sketch, "E140.bottom", {"start": v(5.36, 61) * mm, "end": v(7.26, 61) * mm});
            skLineSegment(sketch, "E140.top", {"start": v(5.36, 53.94) * mm, "end": v(7.26, 53.94) * mm});
            skLineSegment(sketch, "E140.left", {"start": v(5.36, 61) * mm, "end": v(5.36, 53.94) * mm});
            skLineSegment(sketch, "E140.right", {"start": v(7.26, 61) * mm, "end": v(7.26, 53.94) * mm});
            skLineSegment(sketch, "E141.bottom", {"start": v(17.03, 61) * mm, "end": v(14.88, 61) * mm});
            skLineSegment(sketch, "E141.top", {"start": v(17.03, 53.94) * mm, "end": v(14.88, 53.94) * mm});
            skLineSegment(sketch, "E141.left", {"start": v(17.03, 61) * mm, "end": v(17.03, 53.94) * mm});
            skLineSegment(sketch, "E141.right", {"start": v(14.88, 61) * mm, "end": v(14.88, 53.94) * mm});
            skLineSegment(sketch, "E142", {"start": v(5.36, 53.94) * mm, "end": v(17.03, 53.94) * mm});
            skLineSegment(sketch, "E143", {"start": v(17.03, 51.8) * mm, "end": v(5.36, 51.8) * mm});
            skLineSegment(sketch, "E144", {"start": v(5.36, 51.8) * mm, "end": v(5.36, 53.94) * mm});
            skLineSegment(sketch, "E145", {"start": v(17.03, 51.8) * mm, "end": v(17.03, 53.94) * mm});
            skSolve(sketch);
        }
        {
            var Q0;
            Q0 = qSketchRegion(id + "F85", true);
            extrude(context, id + "F86", {"entities" : qUnion([Q0]), "operationType" : NewBodyOperationType.ADD, "depth" : 6.35 * mm, "offsetDistance" : 25.4 * mm});
        }
        {
            var Q0;
            Q0=makeQuery(id+"F86.opExtrude","CAP_FACE",FACE,{"disambiguationData":[OSD([sQuery(id+"F85.wireOp",EDGE,"E140.bottom"),sQuery(id+"F85.wireOp",EDGE,"E140.left"),sQuery(id+"F85.wireOp",EDGE,"E140.right"),sQuery(id+"F85.wireOp",EDGE,"E141.bottom"),sQuery(id+"F85.wireOp",EDGE,"E141.left"),sQuery(id+"F85.wireOp",EDGE,"E141.right"),sQuery(id+"F85.wireOp",EDGE,"E142"),sQuery(id+"F85.wireOp",EDGE,"E143"),sQuery(id+"F85.wireOp",EDGE,"E144"),sQuery(id+"F85.wireOp",EDGE,"E145")])],"isStart":false});
            var sketch = newSketch(context, id + "F87", { "sketchPlane" : qUnion([Q0])});
            skLineSegment(sketch, "E146.bottom", {"start": v(7.26, 61) * mm, "end": v(14.88, 61) * mm});
            skLineSegment(sketch, "E146.top", {"start": v(7.26, 53.94) * mm, "end": v(14.88, 53.94) * mm});
            skLineSegment(sketch, "E146.left", {"start": v(7.26, 61) * mm, "end": v(7.26, 53.94) * mm});
            skLineSegment(sketch, "E146.right", {"start": v(14.88, 61) * mm, "end": v(14.88, 53.94) * mm});
            skSolve(sketch);
        }
        {
            var Q0;
            Q0 = qSketchRegion(id + "F87", true);
            extrude(context, id + "F88", {"entities" : qUnion([Q0]), "operationType" : NewBodyOperationType.ADD, "oppositeDirection" : true, "depth" : 2.03 * mm, "offsetDistance" : 25.4 * mm});
        }
        {
            var Q0;
            Q0=makeQuery(id+"F88.boolean.opBoolean","MERGE",FACE,{"derivedFrom":[makeQuery(id+"F86.opExtrude","CAP_FACE",FACE,{"disambiguationData":[OSD([sQuery(id+"F85.wireOp",EDGE,"E140.bottom"),sQuery(id+"F85.wireOp",EDGE,"E140.left"),sQuery(id+"F85.wireOp",EDGE,"E140.right"),sQuery(id+"F85.wireOp",EDGE,"E141.bottom"),sQuery(id+"F85.wireOp",EDGE,"E141.left"),sQuery(id+"F85.wireOp",EDGE,"E141.right"),sQuery(id+"F85.wireOp",EDGE,"E142"),sQuery(id+"F85.wireOp",EDGE,"E143"),sQuery(id+"F85.wireOp",EDGE,"E144"),sQuery(id+"F85.wireOp",EDGE,"E145")])],"isStart":false}),makeQuery(id+"F88.opExtrude","CAP_FACE",FACE,{"disambiguationData":[OSD([sQuery(id+"F87.wireOp",EDGE,"E146.bottom"),sQuery(id+"F87.wireOp",EDGE,"E146.top"),sQuery(id+"F87.wireOp",EDGE,"E146.left"),sQuery(id+"F87.wireOp",EDGE,"E146.right")])],"isStart":true})]});
            var sketch = newSketch(context, id + "F89", { "sketchPlane" : qUnion([Q0])});
            skLineSegment(sketch, "E147.bottom", {"start": v(7.5, 58.7) * mm, "end": v(8.93, 58.7) * mm});
            skLineSegment(sketch, "E147.top", {"start": v(7.5, 54.42) * mm, "end": v(8.93, 54.42) * mm});
            skLineSegment(sketch, "E147.left", {"start": v(7.5, 58.7) * mm, "end": v(7.5, 54.42) * mm});
            skLineSegment(sketch, "E147.right", {"start": v(8.93, 58.7) * mm, "end": v(8.93, 54.42) * mm});
            skLineSegment(sketch, "E148.bottom", {"start": v(14.88, 59.18) * mm, "end": v(13.7, 59.18) * mm});
            skLineSegment(sketch, "E148.top", {"start": v(14.88, 54.42) * mm, "end": v(13.7, 54.42) * mm});
            skLineSegment(sketch, "E148.left", {"start": v(14.88, 59.18) * mm, "end": v(14.88, 54.42) * mm});
            skLineSegment(sketch, "E148.right", {"start": v(13.7, 59.18) * mm, "end": v(13.7, 54.42) * mm});
            skSolve(sketch);
        }
        {
            var Q0;
            Q0 = qSketchRegion(id + "F89", true);
            extrude(context, id + "F90", {"entities" : qUnion([Q0]), "operationType" : NewBodyOperationType.REMOVE, "oppositeDirection" : true, "depth" : 2.03 * mm, "offsetDistance" : 25.4 * mm});
        }
        {
            var Q0;
            Q0=makeQuery(id+"F86.opExtrude","SWEPT_FACE",FACE,{"disambiguationData":[OSD([sQuery(id+"F85.wireOp",EDGE,"E141.left"),sQuery(id+"F85.wireOp",EDGE,"E145")])]});
            var sketch = newSketch(context, id + "F91", { "sketchPlane" : qUnion([Q0])});
            skLineSegment(sketch, "E149.bottom", {"start": v(-39.65, 58.94) * mm, "end": v(-37.98, 58.94) * mm});
            skLineSegment(sketch, "E149.top", {"start": v(-39.65, 53.7) * mm, "end": v(-37.98, 53.7) * mm});
            skLineSegment(sketch, "E149.left", {"start": v(-39.65, 58.94) * mm, "end": v(-39.65, 53.7) * mm});
            skLineSegment(sketch, "E149.right", {"start": v(-37.98, 58.94) * mm, "end": v(-37.98, 53.7) * mm});
            skSolve(sketch);
        }
        {
            var Q0;
            Q0 = qSketchRegion(id + "F91", true);
            extrude(context, id + "F92", {"entities" : qUnion([Q0]), "operationType" : NewBodyOperationType.REMOVE, "oppositeDirection" : true, "depth" : 2.3 * mm, "offsetDistance" : 25.4 * mm});
        }
        {
            var Q0;
            Q0=makeQuery(id+"F86.opExtrude","SWEPT_FACE",FACE,{"disambiguationData":[OSD([sQuery(id+"F85.wireOp",EDGE,"E140.left"),sQuery(id+"F85.wireOp",EDGE,"E144")])]});
            var sketch = newSketch(context, id + "F93", { "sketchPlane" : qUnion([Q0])});
            skPoint(sketch, "E150.oppositeSnap0", {"position": v(38.26, 51.8) * mm});
            skLineSegment(sketch, "E150.bottom", {"start": v(36.79, 59.18) * mm, "end": v(38.26, 59.18) * mm});
            skLineSegment(sketch, "E150.top", {"start": v(36.79, 53.7) * mm, "end": v(38.26, 53.7) * mm});
            skLineSegment(sketch, "E150.left", {"start": v(36.79, 59.18) * mm, "end": v(36.79, 53.7) * mm});
            skLineSegment(sketch, "E150.right", {"start": v(38.26, 59.18) * mm, "end": v(38.26, 53.7) * mm});
            skSolve(sketch);
        }
        {
            var Q0;
            Q0 = qSketchRegion(id + "F93", true);
            extrude(context, id + "F94", {"entities" : qUnion([Q0]), "operationType" : NewBodyOperationType.REMOVE, "oppositeDirection" : true, "depth" : 2.3 * mm, "offsetDistance" : 25.4 * mm});
        }
        {
            var Q0;
            Q0=makeQuery(id+"F68.boolean.opBoolean","MERGE",FACE,{"derivedFrom":[makeQuery(id+"F66.boolean.opBoolean","MERGE",FACE,{"derivedFrom":[makeQuery(id+"F64.boolean.opBoolean","MERGE",FACE,{"derivedFrom":[makeQuery(id+"F56.opExtrude","CAP_FACE",FACE,{"disambiguationData":[OSD([sQuery(id+"F55.wireOp",EDGE,"E94.bottom"),sQuery(id+"F55.wireOp",EDGE,"E94.top"),sQuery(id+"F55.wireOp",EDGE,"E94.left"),sQuery(id+"F55.wireOp",EDGE,"E94.right")])],"isStart":false}),makeQuery(id+"F64.opExtrude","SWEPT_FACE",FACE,{"disambiguationData":[OSD([sQuery(id+"F63.wireOp",EDGE,"E106.left")])]})]}),makeQuery(id+"F66.opExtrude","SWEPT_FACE",FACE,{"disambiguationData":[OSD([sQuery(id+"F65.wireOp",EDGE,"E107.right")])]}),makeQuery(id+"F66.opExtrude","SWEPT_FACE",FACE,{"disambiguationData":[OSD([sQuery(id+"F65.wireOp",EDGE,"E108.right")])]})]}),makeQuery(id+"F68.opExtrude","SWEPT_FACE",FACE,{"disambiguationData":[OSD([sQuery(id+"F67.wireOp",EDGE,"E109.left")])]})]});
            var sketch = newSketch(context, id + "F95", { "sketchPlane" : qUnion([Q0])});
            skPoint(sketch, "E151.oppositeSnap0", {"position": v(34.2, -8.13) * mm});
            skLineSegment(sketch, "E151.bottom", {"start": v(39.23, 42.28) * mm, "end": v(34.2, 42.28) * mm});
            skLineSegment(sketch, "E151.top", {"start": v(39.23, 11.8) * mm, "end": v(34.2, 11.8) * mm});
            skLineSegment(sketch, "E151.left", {"start": v(39.23, 42.28) * mm, "end": v(39.23, 11.8) * mm});
            skLineSegment(sketch, "E151.right", {"start": v(34.2, 42.28) * mm, "end": v(34.2, 11.8) * mm});
            skSolve(sketch);
        }
        {
            var Q0;
            Q0 = qSketchRegion(id + "F95", true);
            extrude(context, id + "F96", {"entities" : qUnion([Q0]), "operationType" : NewBodyOperationType.REMOVE, "oppositeDirection" : true, "depth" : 3.05 * mm, "offsetDistance" : 25.4 * mm});
        }
        {
            var Q0;
            Q0=makeQuery(id+"F68.boolean.opBoolean","MERGE",FACE,{"derivedFrom":[makeQuery(id+"F66.boolean.opBoolean","MERGE",FACE,{"derivedFrom":[makeQuery(id+"F64.boolean.opBoolean","MERGE",FACE,{"derivedFrom":[makeQuery(id+"F56.opExtrude","CAP_FACE",FACE,{"disambiguationData":[OSD([sQuery(id+"F55.wireOp",EDGE,"E94.bottom"),sQuery(id+"F55.wireOp",EDGE,"E94.top"),sQuery(id+"F55.wireOp",EDGE,"E94.left"),sQuery(id+"F55.wireOp",EDGE,"E94.right")])],"isStart":false}),makeQuery(id+"F64.opExtrude","SWEPT_FACE",FACE,{"disambiguationData":[OSD([sQuery(id+"F63.wireOp",EDGE,"E106.left")])]})]}),makeQuery(id+"F66.opExtrude","SWEPT_FACE",FACE,{"disambiguationData":[OSD([sQuery(id+"F65.wireOp",EDGE,"E107.right")])]}),makeQuery(id+"F66.opExtrude","SWEPT_FACE",FACE,{"disambiguationData":[OSD([sQuery(id+"F65.wireOp",EDGE,"E108.right")])]})]}),makeQuery(id+"F68.opExtrude","SWEPT_FACE",FACE,{"disambiguationData":[OSD([sQuery(id+"F67.wireOp",EDGE,"E109.left")])]})]});
            var sketch = newSketch(context, id + "F97", { "sketchPlane" : qUnion([Q0])});
            skLineSegment(sketch, "E152.bottom", {"start": v(36.71, 11.8) * mm, "end": v(39.23, 11.8) * mm});
            skLineSegment(sketch, "E152.top", {"start": v(36.71, -8.13) * mm, "end": v(39.23, -8.13) * mm});
            skLineSegment(sketch, "E152.left", {"start": v(36.71, 11.8) * mm, "end": v(36.71, -8.13) * mm});
            skLineSegment(sketch, "E152.right", {"start": v(39.23, 11.8) * mm, "end": v(39.23, -8.13) * mm});
            skSolve(sketch);
        }
        {
            var Q0;
            Q0 = qSketchRegion(id + "F97", true);
            extrude(context, id + "F98", {"entities" : qUnion([Q0]), "operationType" : NewBodyOperationType.REMOVE, "oppositeDirection" : true, "depth" : 1.52 * mm, "offsetDistance" : 25.4 * mm});
        }
        {
            var Q0;
            Q0=makeQuery(id+"F60.opExtrude","CAP_FACE",FACE,{"disambiguationData":[OSD([sQuery(id+"F59.wireOp",EDGE,"E99.bottom"),sQuery(id+"F59.wireOp",EDGE,"E99.top"),sQuery(id+"F59.wireOp",EDGE,"E99.left"),sQuery(id+"F59.wireOp",EDGE,"E99.right")])],"isStart":false});
            var sketch = newSketch(context, id + "F99", { "sketchPlane" : qUnion([Q0])});
            skLineSegment(sketch, "E153.bottom", {"start": v(-25.43, 4.52) * mm, "end": v(-21.4, 4.52) * mm});
            skLineSegment(sketch, "E153.top", {"start": v(-25.43, 0) * mm, "end": v(-21.4, 0) * mm});
            skLineSegment(sketch, "E153.left", {"start": v(-25.43, 4.52) * mm, "end": v(-25.43, 0) * mm});
            skLineSegment(sketch, "E153.right", {"start": v(-21.4, 4.52) * mm, "end": v(-21.4, 0) * mm});
            skSolve(sketch);
        }
        {
            var Q0;
            Q0 = qSketchRegion(id + "F99", true);
            extrude(context, id + "F100", {"entities" : qUnion([Q0]), "operationType" : NewBodyOperationType.ADD, "depth" : 25.4 * mm, "offsetDistance" : 25.4 * mm});
        }
        {
            var Q0;
            Q0=makeQuery(id+"F100.opExtrude","SWEPT_FACE",FACE,{"disambiguationData":[OSD([sQuery(id+"F99.wireOp",EDGE,"E153.right")])]});
            var sketch = newSketch(context, id + "F101", { "sketchPlane" : qUnion([Q0])});
            skLineSegment(sketch, "E154.bottom", {"start": v(0, 129.72) * mm, "end": v(44, 129.72) * mm});
            skLineSegment(sketch, "E154.top", {"start": v(0, 115.42) * mm, "end": v(44, 115.42) * mm});
            skLineSegment(sketch, "E154.left", {"start": v(0, 129.72) * mm, "end": v(0, 115.42) * mm});
            skLineSegment(sketch, "E154.right", {"start": v(44, 129.72) * mm, "end": v(44, 115.42) * mm});
            skSolve(sketch);
        }
        {
            var Q0;
            Q0 = qSketchRegion(id + "F101", true);
            extrude(context, id + "F102", {"entities" : qUnion([Q0]), "operationType" : NewBodyOperationType.ADD, "oppositeDirection" : true, "depth" : 4.32 * mm, "offsetDistance" : 25.4 * mm});
        }
        {
            var Q0;
            Q0=makeQuery(id+"F102.boolean.opBoolean","MERGE",FACE,{"derivedFrom":[makeQuery(id+"F100.opExtrude","SWEPT_FACE",FACE,{"disambiguationData":[OSD([sQuery(id+"F99.wireOp",EDGE,"E153.right")])]}),makeQuery(id+"F102.opExtrude","CAP_FACE",FACE,{"disambiguationData":[OSD([sQuery(id+"F101.wireOp",EDGE,"E154.bottom"),sQuery(id+"F101.wireOp",EDGE,"E154.top"),sQuery(id+"F101.wireOp",EDGE,"E154.left"),sQuery(id+"F101.wireOp",EDGE,"E154.right")])],"isStart":true})]});
            var sketch = newSketch(context, id + "F103", { "sketchPlane" : qUnion([Q0])});
            skLineSegment(sketch, "E155.bottom", {"start": v(8.97, 129.72) * mm, "end": v(11.4, 129.72) * mm});
            skLineSegment(sketch, "E155.top", {"start": v(8.97, 115.42) * mm, "end": v(11.4, 115.42) * mm});
            skLineSegment(sketch, "E155.left", {"start": v(8.97, 129.72) * mm, "end": v(8.97, 115.42) * mm});
            skLineSegment(sketch, "E155.right", {"start": v(11.4, 129.72) * mm, "end": v(11.4, 115.42) * mm});
            skLineSegment(sketch, "E156.bottom", {"start": v(28.44, 129.72) * mm, "end": v(31.65, 129.72) * mm});
            skLineSegment(sketch, "E156.top", {"start": v(28.44, 122.32) * mm, "end": v(31.65, 122.32) * mm});
            skLineSegment(sketch, "E156.left", {"start": v(28.44, 129.72) * mm, "end": v(28.44, 122.32) * mm});
            skLineSegment(sketch, "E156.right", {"start": v(31.65, 129.72) * mm, "end": v(31.65, 122.32) * mm});
            skLineSegment(sketch, "E157.bottom", {"start": v(28.44, 122.32) * mm, "end": v(30.11, 122.32) * mm});
            skLineSegment(sketch, "E157.top", {"start": v(28.44, 115.42) * mm, "end": v(30.11, 115.42) * mm});
            skLineSegment(sketch, "E157.left", {"start": v(28.44, 122.32) * mm, "end": v(28.44, 115.42) * mm});
            skLineSegment(sketch, "E157.right", {"start": v(30.11, 122.32) * mm, "end": v(30.11, 115.42) * mm});
            skSolve(sketch);
        }
        {
            var Q0;
            Q0 = qSketchRegion(id + "F103", true);
            extrude(context, id + "F104", {"entities" : qUnion([Q0]), "operationType" : NewBodyOperationType.REMOVE, "oppositeDirection" : true, "depth" : 2.3 * mm, "offsetDistance" : 25.4 * mm});
        }
        {
            var Q0;
            {var subQ0=sQuery(id+"F101.wireOp",EDGE,"E154.bottom");var subQ1=sQuery(id+"F101.wireOp",EDGE,"E154.top");var subQ2=sQuery(id+"F99.wireOp",EDGE,"E153.right");Q0=makeQuery(id+"F104.boolean.opBoolean","SPLIT",FACE,{"disambiguationData":[TD([makeQuery(id+"F104.opExtrude","SWEPT_FACE",FACE,{"disambiguationData":[OSD([sQuery(id+"F103.wireOp",EDGE,"E155.right")])]})])],"derivedFrom":makeQuery(id+"F102.boolean.opBoolean","MERGE",FACE,{"derivedFrom":[makeQuery(id+"F100.opExtrude","SWEPT_FACE",FACE,{"disambiguationData":[OSD([subQ2])]}),makeQuery(id+"F102.opExtrude","CAP_FACE",FACE,{"disambiguationData":[OSD([subQ0,subQ1,sQuery(id+"F101.wireOp",EDGE,"E154.left"),sQuery(id+"F101.wireOp",EDGE,"E154.right")])],"isStart":true})]})});}
            var sketch = newSketch(context, id + "F105", { "sketchPlane" : qUnion([Q0])});
            skLineSegment(sketch, "E158.bottom", {"start": v(15, 129.72) * mm, "end": v(22.68, 129.72) * mm});
            skLineSegment(sketch, "E158.top", {"start": v(15, 121.56) * mm, "end": v(22.68, 121.56) * mm});
            skLineSegment(sketch, "E158.left", {"start": v(15, 129.72) * mm, "end": v(15, 121.56) * mm});
            skLineSegment(sketch, "E158.right", {"start": v(22.68, 129.72) * mm, "end": v(22.68, 121.56) * mm});
            skLineSegment(sketch, "E159.bottom", {"start": v(22.68, 121.56) * mm, "end": v(18.32, 121.56) * mm});
            skLineSegment(sketch, "E159.top", {"start": v(22.68, 115.42) * mm, "end": v(18.32, 115.42) * mm});
            skLineSegment(sketch, "E159.left", {"start": v(22.68, 121.56) * mm, "end": v(22.68, 115.42) * mm});
            skLineSegment(sketch, "E159.right", {"start": v(18.32, 121.56) * mm, "end": v(18.32, 115.42) * mm});
            skSolve(sketch);
        }
        {
            var Q0;
            Q0 = qSketchRegion(id + "F105", true);
            extrude(context, id + "F106", {"entities" : qUnion([Q0]), "operationType" : NewBodyOperationType.ADD, "depth" : 2.3 * mm, "offsetDistance" : 25.4 * mm});
        }
        {
            var Q0;
            Q0=makeQuery(id+"F106.boolean.opBoolean","MERGE",FACE,{"derivedFrom":[makeQuery(id+"F102.boolean.opBoolean","MERGE",FACE,{"derivedFrom":[makeQuery(id+"F100.opExtrude","CAP_FACE",FACE,{"disambiguationData":[OSD([sQuery(id+"F99.wireOp",EDGE,"E153.bottom"),sQuery(id+"F99.wireOp",EDGE,"E153.top"),sQuery(id+"F99.wireOp",EDGE,"E153.left"),sQuery(id+"F99.wireOp",EDGE,"E153.right")])],"isStart":false}),makeQuery(id+"F102.opExtrude","SWEPT_FACE",FACE,{"disambiguationData":[OSD([sQuery(id+"F101.wireOp",EDGE,"E154.bottom")])]})]}),makeQuery(id+"F106.opExtrude","SWEPT_FACE",FACE,{"disambiguationData":[OSD([sQuery(id+"F105.wireOp",EDGE,"E158.bottom")])]})]});
            var sketch = newSketch(context, id + "F107", { "sketchPlane" : qUnion([Q0])});
            skLineSegment(sketch, "E160.bottom", {"start": v(-25.73, 13.3) * mm, "end": v(-23.82, 13.3) * mm});
            skLineSegment(sketch, "E160.top", {"start": v(-25.73, 15.35) * mm, "end": v(-23.82, 15.35) * mm});
            skLineSegment(sketch, "E160.left", {"start": v(-25.73, 13.3) * mm, "end": v(-25.73, 15.35) * mm});
            skLineSegment(sketch, "E160.right", {"start": v(-23.82, 13.3) * mm, "end": v(-23.82, 15.35) * mm});
            skLineSegment(sketch, "E161.bottom", {"start": v(-25.73, 15.35) * mm, "end": v(-23.07, 15.35) * mm});
            skLineSegment(sketch, "E161.top", {"start": v(-25.73, 22.13) * mm, "end": v(-23.07, 22.13) * mm});
            skLineSegment(sketch, "E161.left", {"start": v(-25.73, 15.35) * mm, "end": v(-25.73, 22.13) * mm});
            skLineSegment(sketch, "E161.right", {"start": v(-23.07, 15.35) * mm, "end": v(-23.07, 22.13) * mm});
            skSolve(sketch);
        }
        {
            var Q0;
            Q0 = qSketchRegion(id + "F107", true);
            extrude(context, id + "F108", {"entities" : qUnion([Q0]), "operationType" : NewBodyOperationType.REMOVE, "oppositeDirection" : true, "depth" : 16 * mm, "offsetDistance" : 25.4 * mm});
        }
        {
            var Q0;
            {var subQ0=sQuery(id+"F101.wireOp",EDGE,"E154.right");var subQ1=sQuery(id+"F101.wireOp",EDGE,"E154.bottom");var subQ2=sQuery(id+"F101.wireOp",EDGE,"E154.top");Q0=makeQuery(id+"F108.boolean.opBoolean","SPLIT",FACE,{"disambiguationData":[TD([makeQuery(id+"F102.opExtrude","SWEPT_FACE",FACE,{"disambiguationData":[OSD([subQ0])]})])],"derivedFrom":makeQuery(id+"F102.opExtrude","CAP_FACE",FACE,{"disambiguationData":[OSD([subQ1,subQ2,sQuery(id+"F101.wireOp",EDGE,"E154.left"),subQ0])],"isStart":false})});}
            var sketch = newSketch(context, id + "F109", { "sketchPlane" : qUnion([Q0])});
            skLineSegment(sketch, "E162.bottom", {"start": v(-33.06, 129.72) * mm, "end": v(-27.23, 129.72) * mm});
            skLineSegment(sketch, "E162.top", {"start": v(-33.06, 115.42) * mm, "end": v(-27.23, 115.42) * mm});
            skLineSegment(sketch, "E162.left", {"start": v(-33.06, 129.72) * mm, "end": v(-33.06, 115.42) * mm});
            skLineSegment(sketch, "E162.right", {"start": v(-27.23, 129.72) * mm, "end": v(-27.23, 115.42) * mm});
            skSolve(sketch);
        }
        {
            var Q0;
            Q0 = qSketchRegion(id + "F109", true);
            extrude(context, id + "F110", {"entities" : qUnion([Q0]), "operationType" : NewBodyOperationType.ADD, "depth" : 3.05 * mm, "offsetDistance" : 25.4 * mm});
        }
        {
            var Q0;
            {var subQ0=sQuery(id+"F10.wireOp",EDGE,"E19.bottom");var subQ1=makeQuery(id+"F11.opExtrude","SWEPT_FACE",FACE,{"disambiguationData":[OSD([subQ0])]});var subQ2=sQuery(id+"F2.wireOp",EDGE,"E1");var subQ3=makeQuery(id+"F3.boolean.opBoolean","COPY",FACE,{"derivedFrom":makeQuery(id+"F3.opExtrude","SWEPT_FACE",FACE,{"disambiguationData":[OSD([subQ2])]})});var subQ4=makeQuery(id+"F50.opExtrude","SWEPT_FACE",FACE,{"disambiguationData":[OSD([sQuery(id+"F49.wireOp",EDGE,"E91.top")])]});var subQ5=sQuery(id+"F47.wireOp",EDGE,"E89.left");var subQ6=sQuery(id+"F47.wireOp",EDGE,"E89.top");var subQ7=makeQuery(id+"F48.opExtrude","SWEPT_FACE",FACE,{"disambiguationData":[OSD([subQ6])]});var subQ8=sQuery(id+"F47.wireOp",EDGE,"E89.right");var subQ9=sQuery(id+"F10.wireOp",EDGE,"E18.left");var subQ10=makeQuery(id+"F11.opExtrude","SWEPT_FACE",FACE,{"disambiguationData":[OSD([subQ9])]});var subQ11=sQuery(id+"F47.wireOp",EDGE,"E88.right");var subQ12=sQuery(id+"F47.wireOp",EDGE,"E88.left");var subQ13=sQuery(id+"F47.wireOp",EDGE,"E88.top");var subQ14=makeQuery(id+"F48.opExtrude","SWEPT_FACE",FACE,{"disambiguationData":[OSD([subQ13])]});var subQ15=makeQuery(id+"F40.opExtrude","SWEPT_FACE",FACE,{"disambiguationData":[OSD([sQuery(id+"F39.wireOp",EDGE,"E63.bottom"),sQuery(id+"F39.wireOp",EDGE,"E64.bottom"),sQuery(id+"F39.wireOp",EDGE,"E65.bottom")])]});var subQ16=makeQuery(id+"F40.opExtrude","SWEPT_FACE",FACE,{"disambiguationData":[OSD([sQuery(id+"F39.wireOp",EDGE,"E63.right")])]});var subQ17=makeQuery(id+"F40.opExtrude","SWEPT_FACE",FACE,{"disambiguationData":[OSD([sQuery(id+"F39.wireOp",EDGE,"E63.top"),sQuery(id+"F39.wireOp",EDGE,"E64.top"),sQuery(id+"F39.wireOp",EDGE,"E66.bottom")])]});var subQ18=sQuery(id+"F10.wireOp",EDGE,"E18.right");var subQ19=sQuery(id+"F10.wireOp",EDGE,"E18.bottom");var subQ20=sQuery(id+"F0.wireOp",EDGE,"E0.right");var subQ21=sQuery(id+"F0.wireOp",EDGE,"E0.bottom");var subQ23=sQuery(id+"F10.wireOp",EDGE,"E20.bottom");var subQ24=makeQuery(id+"F11.opExtrude","SWEPT_FACE",FACE,{"disambiguationData":[OSD([subQ18]),TDD([makeQuery(id+"F10.imprint","IMPRINT",EDGE,{"disambiguationData":[TD([[makeQuery(id+"F10.imprint","INTERSECT",VERTEX,{"derivedFrom":[subQ18,subQ23,sQuery(id+"F10.wireOp",EDGE,"E20.left")]}),1.0]])],"derivedFrom":subQ18})])]});var subQ25=sQuery(id+"F17.wireOp",EDGE,"E34.bottom");var subQ26=sQuery(id+"F17.wireOp",EDGE,"E33.bottom");var subQ27=sQuery(id+"F17.wireOp",EDGE,"E32.bottom");var subQ28=makeQuery(id+"F18.opExtrude","SWEPT_FACE",FACE,{"disambiguationData":[OSD([subQ27,subQ26,subQ25])]});var subQ29=sQuery(id+"F25.wireOp",EDGE,"E44.bottom");var subQ30=makeQuery(id+"F26.opExtrude","SWEPT_FACE",FACE,{"disambiguationData":[OSD([subQ29])]});var subQ31=makeQuery(id+"F3.boolean.opBoolean","COPY",FACE,{"derivedFrom":makeQuery(id+"F3.opExtrude","CAP_FACE",FACE,{"disambiguationData":[OSD([subQ21,subQ20,subQ2,sQuery(id+"F2.wireOp",EDGE,"E2"),sQuery(id+"F2.wireOp",EDGE,"E3"),sQuery(id+"F2.wireOp",EDGE,"E4"),sQuery(id+"F2.wireOp",EDGE,"E5"),sQuery(id+"F2.wireOp",EDGE,"E6"),sQuery(id+"F2.wireOp",EDGE,"E7"),sQuery(id+"F2.wireOp",EDGE,"E8"),sQuery(id+"F2.wireOp",EDGE,"E9"),sQuery(id+"F2.wireOp",EDGE,"E10"),sQuery(id+"F2.wireOp",EDGE,"E11"),sQuery(id+"F2.wireOp",EDGE,"E12"),sQuery(id+"F2.wireOp",EDGE,"E13"),sQuery(id+"F2.wireOp",EDGE,"E14")])],"isStart":false})});var subQ32=sQuery(id+"F17.wireOp",EDGE,"E32.right");var subQ33=makeQuery(id+"F18.opExtrude","SWEPT_FACE",FACE,{"disambiguationData":[OSD([subQ32])]});var subQ34=sQuery(id+"F10.wireOp",EDGE,"E19.right");var subQ35=sQuery(id+"F10.wireOp",EDGE,"E19.left");var subQ36=makeQuery(id+"F11.opExtrude","CAP_FACE",FACE,{"disambiguationData":[OSD([subQ19,sQuery(id+"F10.wireOp",EDGE,"E18.top"),subQ9,subQ18,subQ0,sQuery(id+"F10.wireOp",EDGE,"E19.top"),subQ35,subQ34,subQ23,sQuery(id+"F10.wireOp",EDGE,"E20.top"),sQuery(id+"F10.wireOp",EDGE,"E21.bottom"),sQuery(id+"F10.wireOp",EDGE,"E21.top"),sQuery(id+"F10.wireOp",EDGE,"E22.bottom"),sQuery(id+"F10.wireOp",EDGE,"E22.top"),sQuery(id+"F10.wireOp",EDGE,"E23.bottom"),sQuery(id+"F10.wireOp",EDGE,"E23.top"),sQuery(id+"F10.wireOp",EDGE,"E24.bottom"),sQuery(id+"F10.wireOp",EDGE,"E24.top")])],"isStart":false});var subQ37=makeQuery(id+"F18.opExtrude","CAP_FACE",FACE,{"disambiguationData":[OSD([sQuery(id+"F17.wireOp",EDGE,"E28.left"),sQuery(id+"F17.wireOp",EDGE,"E28.right"),sQuery(id+"F17.wireOp",EDGE,"E29.bottom"),sQuery(id+"F17.wireOp",EDGE,"E29.top"),sQuery(id+"F17.wireOp",EDGE,"E29.left"),sQuery(id+"F17.wireOp",EDGE,"E29.right"),sQuery(id+"F17.wireOp",EDGE,"E30.left"),sQuery(id+"F17.wireOp",EDGE,"E30.right"),sQuery(id+"F17.wireOp",EDGE,"E31.bottom"),sQuery(id+"F17.wireOp",EDGE,"E31.top"),sQuery(id+"F17.wireOp",EDGE,"E31.left"),sQuery(id+"F17.wireOp",EDGE,"E31.right"),subQ27,sQuery(id+"F17.wireOp",EDGE,"E32.top"),sQuery(id+"F17.wireOp",EDGE,"E32.left"),subQ32,subQ26,sQuery(id+"F17.wireOp",EDGE,"E33.top"),sQuery(id+"F17.wireOp",EDGE,"E33.left"),sQuery(id+"F17.wireOp",EDGE,"E33.right"),subQ25,sQuery(id+"F17.wireOp",EDGE,"E34.top"),sQuery(id+"F17.wireOp",EDGE,"E34.left"),sQuery(id+"F17.wireOp",EDGE,"E34.right")])],"isStart":false});var subQ38=makeQuery(id+"F1.opExtrude","CAP_FACE",FACE,{"disambiguationData":[OSD([subQ21,sQuery(id+"F0.wireOp",EDGE,"E0.top"),sQuery(id+"F0.wireOp",EDGE,"E0.left"),subQ20])],"isStart":false});var subQ39=makeQuery(id+"F11.opExtrude","SWEPT_FACE",FACE,{"disambiguationData":[OSD([subQ19])]});var subQ40=sQuery(id+"F25.wireOp",EDGE,"E44.left");var subQ41=makeQuery(id+"F26.opExtrude","SWEPT_FACE",FACE,{"disambiguationData":[OSD([subQ40])]});var subQ42=makeQuery(id+"F1.opExtrude","SWEPT_FACE",FACE,{"disambiguationData":[OSD([subQ20])]});var subQ43=makeQuery(id+"F42.opExtrude","SWEPT_FACE",FACE,{"disambiguationData":[OSD([sQuery(id+"F41.wireOp",EDGE,"E67.bottom")])]});var subQ44=makeQuery(id+"F40.opExtrude","SWEPT_FACE",FACE,{"disambiguationData":[OSD([sQuery(id+"F39.wireOp",EDGE,"E64.left")])]});var subQ45=sQuery(id+"F25.wireOp",EDGE,"E44.right");var subQ46=makeQuery(id+"F26.opExtrude","CAP_FACE",FACE,{"disambiguationData":[OSD([sQuery(id+"F25.wireOp",EDGE,"E41.left"),sQuery(id+"F25.wireOp",EDGE,"E41.right"),sQuery(id+"F25.wireOp",EDGE,"E42.left"),sQuery(id+"F25.wireOp",EDGE,"E42.right"),sQuery(id+"F25.wireOp",EDGE,"E43.bottom"),sQuery(id+"F25.wireOp",EDGE,"E43.top"),sQuery(id+"F25.wireOp",EDGE,"E43.left"),sQuery(id+"F25.wireOp",EDGE,"E43.right"),subQ29,sQuery(id+"F25.wireOp",EDGE,"E44.top"),subQ40,subQ45,sQuery(id+"F25.wireOp",EDGE,"E45.bottom"),sQuery(id+"F25.wireOp",EDGE,"E45.top"),sQuery(id+"F25.wireOp",EDGE,"E45.left"),sQuery(id+"F25.wireOp",EDGE,"E45.right"),sQuery(id+"F25.wireOp",EDGE,"E46.bottom"),sQuery(id+"F25.wireOp",EDGE,"E46.top"),sQuery(id+"F25.wireOp",EDGE,"E46.left"),sQuery(id+"F25.wireOp",EDGE,"E46.right")])],"isStart":false});var subQ47=makeQuery(id+"F11.opExtrude","SWEPT_FACE",FACE,{"disambiguationData":[OSD([subQ34])]});var subQ48=makeQuery(id+"F1.opExtrude","SWEPT_FACE",FACE,{"disambiguationData":[OSD([subQ21])]});var subQ49=makeQuery(id+"F11.opExtrude","SWEPT_FACE",FACE,{"disambiguationData":[OSD([subQ35]),TDD([makeQuery(id+"F10.imprint","IMPRINT",EDGE,{"disambiguationData":[TD([[makeQuery(id+"F10.imprint","INTERSECT",VERTEX,{"derivedFrom":[subQ35,subQ23,sQuery(id+"F10.wireOp",EDGE,"E20.right")]}),1.0]])],"derivedFrom":subQ35})])]});var subQ50=sQuery(id+"F37.wireOp",EDGE,"E57");var subQ51=makeQuery(id+"F38.boolean.opBoolean","COPY",FACE,{"derivedFrom":makeQuery(id+"F38.opExtrude","CAP_FACE",FACE,{"disambiguationData":[OSD([subQ21,subQ20,subQ50,sQuery(id+"F37.wireOp",EDGE,"E58"),sQuery(id+"F37.wireOp",EDGE,"E59"),sQuery(id+"F37.wireOp",EDGE,"E60"),sQuery(id+"F37.wireOp",EDGE,"E61"),sQuery(id+"F37.wireOp",EDGE,"E62")])],"isStart":false})});var subQ52=makeQuery(id+"F26.opExtrude","SWEPT_FACE",FACE,{"disambiguationData":[OSD([subQ45])]});var subQ53=makeQuery(id+"F38.boolean.opBoolean","COPY",FACE,{"derivedFrom":makeQuery(id+"F38.opExtrude","SWEPT_FACE",FACE,{"disambiguationData":[OSD([subQ50])]})});var subQ54=makeQuery(id+"F26.boolean.opBoolean","MERGE",FACE,{"derivedFrom":[makeQuery(id+"F18.boolean.opBoolean","MERGE",FACE,{"derivedFrom":[makeQuery(id+"F11.boolean.opBoolean","MERGE",FACE,{"derivedFrom":[subQ48,subQ39,subQ1]}),subQ28]}),subQ30]});Q0=makeQuery(id+"F76.boolean.opBoolean","SPLIT",FACE,{"disambiguationData":[TD([subQ48,subQ38,subQ42,subQ3,subQ31,subQ39,subQ36,subQ10,subQ24,subQ1,subQ49,subQ47,subQ37,subQ28,subQ33,subQ46,subQ30,subQ41,subQ52,subQ53,subQ51,subQ15,subQ17,subQ16,subQ44,subQ43,makeQuery(id+"F42.boolean.opBoolean","COPY",FACE,{"derivedFrom":makeQuery(id+"F42.opExtrude","SWEPT_FACE",FACE,{"disambiguationData":[OSD([sQuery(id+"F41.wireOp",EDGE,"E67.left")])]})}),makeQuery(id+"F42.boolean.opBoolean","COPY",FACE,{"derivedFrom":makeQuery(id+"F42.opExtrude","SWEPT_FACE",FACE,{"disambiguationData":[OSD([sQuery(id+"F41.wireOp",EDGE,"E67.right")])]})}),subQ14,subQ7,makeQuery(id+"F48.boolean.opBoolean","COPY",FACE,{"derivedFrom":makeQuery(id+"F48.opExtrude","CAP_FACE",FACE,{"disambiguationData":[OSD([sQuery(id+"F47.wireOp",EDGE,"E88.bottom"),subQ13,subQ12,subQ11])],"isStart":false})}),makeQuery(id+"F48.boolean.opBoolean","COPY",FACE,{"derivedFrom":makeQuery(id+"F48.opExtrude","SWEPT_FACE",FACE,{"disambiguationData":[OSD([subQ12])]})}),makeQuery(id+"F48.boolean.opBoolean","COPY",FACE,{"derivedFrom":makeQuery(id+"F48.opExtrude","SWEPT_FACE",FACE,{"disambiguationData":[OSD([subQ11])]})}),makeQuery(id+"F48.boolean.opBoolean","COPY",FACE,{"derivedFrom":makeQuery(id+"F48.opExtrude","CAP_FACE",FACE,{"disambiguationData":[OSD([sQuery(id+"F47.wireOp",EDGE,"E89.bottom"),subQ6,subQ5,subQ8])],"isStart":false})}),makeQuery(id+"F48.boolean.opBoolean","COPY",FACE,{"derivedFrom":makeQuery(id+"F48.opExtrude","SWEPT_FACE",FACE,{"disambiguationData":[OSD([subQ5])]})}),makeQuery(id+"F48.boolean.opBoolean","COPY",FACE,{"derivedFrom":makeQuery(id+"F48.opExtrude","SWEPT_FACE",FACE,{"disambiguationData":[OSD([subQ8])]})}),subQ4,makeQuery(id+"F52.opExtrude","SWEPT_FACE",FACE,{"disambiguationData":[OSD([sQuery(id+"F51.wireOp",EDGE,"E92.bottom")])]}),makeQuery(id+"F52.opExtrude","SWEPT_FACE",FACE,{"disambiguationData":[OSD([sQuery(id+"F51.wireOp",EDGE,"E92.left")])]}),makeQuery(id+"F52.opExtrude","SWEPT_FACE",FACE,{"disambiguationData":[OSD([sQuery(id+"F51.wireOp",EDGE,"E92.right")])]}),makeQuery(id+"F54.opExtrude","SWEPT_FACE",FACE,{"disambiguationData":[OSD([sQuery(id+"F53.wireOp",EDGE,"E93.right")])]}),makeQuery(id+"F56.opExtrude","SWEPT_FACE",FACE,{"disambiguationData":[OSD([sQuery(id+"F55.wireOp",EDGE,"E94.left")])]}),makeQuery(id+"F76.opExtrude","SWEPT_FACE",FACE,{"disambiguationData":[OSD([sQuery(id+"F75.wireOp",EDGE,"E120")])]}),makeQuery(id+"F76.opExtrude","SWEPT_FACE",FACE,{"disambiguationData":[OSD([sQuery(id+"F75.wireOp",EDGE,"E121")])]}),makeQuery(id+"F76.opExtrude","SWEPT_FACE",FACE,{"disambiguationData":[OSD([sQuery(id+"F75.wireOp",EDGE,"E122")])]}),makeQuery(id+"F76.opExtrude","SWEPT_FACE",FACE,{"disambiguationData":[OSD([sQuery(id+"F75.wireOp",EDGE,"E123")])]}),makeQuery(id+"F76.opExtrude","SWEPT_FACE",FACE,{"disambiguationData":[OSD([sQuery(id+"F75.wireOp",EDGE,"E124")])]}),makeQuery(id+"F76.opExtrude","SWEPT_FACE",FACE,{"disambiguationData":[OSD([sQuery(id+"F75.wireOp",EDGE,"E126")])]}),makeQuery(id+"F76.opExtrude","SWEPT_FACE",FACE,{"disambiguationData":[OSD([sQuery(id+"F75.wireOp",EDGE,"E127"),sQuery(id+"F75.wireOp",EDGE,"E128")])]}),makeQuery(id+"F76.opExtrude","SWEPT_FACE",FACE,{"disambiguationData":[OSD([sQuery(id+"F75.wireOp",EDGE,"E129")])]}),makeQuery(id+"F76.opExtrude","SWEPT_FACE",FACE,{"disambiguationData":[OSD([sQuery(id+"F75.wireOp",EDGE,"E130")])]}),makeQuery(id+"F76.opExtrude","SWEPT_FACE",FACE,{"disambiguationData":[OSD([sQuery(id+"F75.wireOp",EDGE,"E131")])]})])],"derivedFrom":makeQuery(id+"F50.boolean.opBoolean","MERGE",FACE,{"derivedFrom":[makeQuery(id+"F40.boolean.opBoolean","SPLIT",FACE,{"disambiguationData":[TD([makeQuery(id+"F40.opExtrude","SWEPT_FACE",FACE,{"disambiguationData":[OSD([sQuery(id+"F39.wireOp",EDGE,"E63.left")])]})])],"derivedFrom":subQ54}),makeQuery(id+"F48.boolean.opBoolean","MERGE",FACE,{"derivedFrom":[makeQuery(id+"F42.boolean.opBoolean","MERGE",FACE,{"derivedFrom":[makeQuery(id+"F40.boolean.opBoolean","SPLIT",FACE,{"disambiguationData":[TD([subQ42])],"derivedFrom":subQ54}),subQ43]}),subQ14,subQ7]}),subQ4]})});}
            var sketch = newSketch(context, id + "F111", { "sketchPlane" : qUnion([Q0])});
            skLineSegment(sketch, "E163.bottom", {"start": v(10.93, -9.75) * mm, "end": v(20.32, -9.75) * mm});
            skLineSegment(sketch, "E163.top", {"start": v(10.93, -5.53) * mm, "end": v(20.32, -5.53) * mm});
            skLineSegment(sketch, "E163.left", {"start": v(10.93, -9.75) * mm, "end": v(10.93, -5.53) * mm});
            skLineSegment(sketch, "E163.right", {"start": v(20.32, -9.75) * mm, "end": v(20.32, -5.53) * mm});
            skLineSegment(sketch, "E164.bottom", {"start": v(10.93, 8.95) * mm, "end": v(20.32, 8.95) * mm});
            skLineSegment(sketch, "E164.top", {"start": v(10.93, 4.52) * mm, "end": v(20.32, 4.52) * mm});
            skLineSegment(sketch, "E164.left", {"start": v(10.93, 8.95) * mm, "end": v(10.93, 4.52) * mm});
            skLineSegment(sketch, "E164.right", {"start": v(20.32, 8.95) * mm, "end": v(20.32, 4.52) * mm});
            skSolve(sketch);
        }
        {
            var Q0;
            Q0 = qSketchRegion(id + "F111", true);
            extrude(context, id + "F112", {"entities" : qUnion([Q0]), "operationType" : NewBodyOperationType.REMOVE, "oppositeDirection" : true, "depth" : 3.05 * mm, "offsetDistance" : 25.4 * mm});
        }
        {
            var Q0;
            {var subQ0=sQuery(id+"F10.wireOp",EDGE,"E19.bottom");var subQ1=makeQuery(id+"F11.opExtrude","SWEPT_FACE",FACE,{"disambiguationData":[OSD([subQ0])]});var subQ2=sQuery(id+"F2.wireOp",EDGE,"E1");var subQ3=makeQuery(id+"F3.boolean.opBoolean","COPY",FACE,{"derivedFrom":makeQuery(id+"F3.opExtrude","SWEPT_FACE",FACE,{"disambiguationData":[OSD([subQ2])]})});var subQ4=makeQuery(id+"F50.opExtrude","SWEPT_FACE",FACE,{"disambiguationData":[OSD([sQuery(id+"F49.wireOp",EDGE,"E91.top")])]});var subQ5=sQuery(id+"F47.wireOp",EDGE,"E89.left");var subQ6=sQuery(id+"F47.wireOp",EDGE,"E89.top");var subQ7=makeQuery(id+"F48.opExtrude","SWEPT_FACE",FACE,{"disambiguationData":[OSD([subQ6])]});var subQ8=sQuery(id+"F47.wireOp",EDGE,"E89.right");var subQ9=sQuery(id+"F10.wireOp",EDGE,"E18.left");var subQ10=makeQuery(id+"F11.opExtrude","SWEPT_FACE",FACE,{"disambiguationData":[OSD([subQ9])]});var subQ11=sQuery(id+"F47.wireOp",EDGE,"E88.right");var subQ12=sQuery(id+"F47.wireOp",EDGE,"E88.left");var subQ13=sQuery(id+"F47.wireOp",EDGE,"E88.top");var subQ14=makeQuery(id+"F48.opExtrude","SWEPT_FACE",FACE,{"disambiguationData":[OSD([subQ13])]});var subQ15=makeQuery(id+"F40.opExtrude","SWEPT_FACE",FACE,{"disambiguationData":[OSD([sQuery(id+"F39.wireOp",EDGE,"E63.bottom"),sQuery(id+"F39.wireOp",EDGE,"E64.bottom"),sQuery(id+"F39.wireOp",EDGE,"E65.bottom")])]});var subQ16=makeQuery(id+"F40.opExtrude","SWEPT_FACE",FACE,{"disambiguationData":[OSD([sQuery(id+"F39.wireOp",EDGE,"E63.right")])]});var subQ17=makeQuery(id+"F40.opExtrude","SWEPT_FACE",FACE,{"disambiguationData":[OSD([sQuery(id+"F39.wireOp",EDGE,"E63.top"),sQuery(id+"F39.wireOp",EDGE,"E64.top"),sQuery(id+"F39.wireOp",EDGE,"E66.bottom")])]});var subQ18=sQuery(id+"F10.wireOp",EDGE,"E18.right");var subQ19=sQuery(id+"F10.wireOp",EDGE,"E18.bottom");var subQ20=sQuery(id+"F0.wireOp",EDGE,"E0.right");var subQ21=sQuery(id+"F0.wireOp",EDGE,"E0.bottom");var subQ23=sQuery(id+"F10.wireOp",EDGE,"E20.bottom");var subQ24=makeQuery(id+"F11.opExtrude","SWEPT_FACE",FACE,{"disambiguationData":[OSD([subQ18]),TDD([makeQuery(id+"F10.imprint","IMPRINT",EDGE,{"disambiguationData":[TD([[makeQuery(id+"F10.imprint","INTERSECT",VERTEX,{"derivedFrom":[subQ18,subQ23,sQuery(id+"F10.wireOp",EDGE,"E20.left")]}),1.0]])],"derivedFrom":subQ18})])]});var subQ25=sQuery(id+"F17.wireOp",EDGE,"E34.bottom");var subQ26=sQuery(id+"F17.wireOp",EDGE,"E33.bottom");var subQ27=sQuery(id+"F17.wireOp",EDGE,"E32.bottom");var subQ28=makeQuery(id+"F18.opExtrude","SWEPT_FACE",FACE,{"disambiguationData":[OSD([subQ27,subQ26,subQ25])]});var subQ29=sQuery(id+"F25.wireOp",EDGE,"E44.bottom");var subQ30=makeQuery(id+"F26.opExtrude","SWEPT_FACE",FACE,{"disambiguationData":[OSD([subQ29])]});var subQ31=makeQuery(id+"F3.boolean.opBoolean","COPY",FACE,{"derivedFrom":makeQuery(id+"F3.opExtrude","CAP_FACE",FACE,{"disambiguationData":[OSD([subQ21,subQ20,subQ2,sQuery(id+"F2.wireOp",EDGE,"E2"),sQuery(id+"F2.wireOp",EDGE,"E3"),sQuery(id+"F2.wireOp",EDGE,"E4"),sQuery(id+"F2.wireOp",EDGE,"E5"),sQuery(id+"F2.wireOp",EDGE,"E6"),sQuery(id+"F2.wireOp",EDGE,"E7"),sQuery(id+"F2.wireOp",EDGE,"E8"),sQuery(id+"F2.wireOp",EDGE,"E9"),sQuery(id+"F2.wireOp",EDGE,"E10"),sQuery(id+"F2.wireOp",EDGE,"E11"),sQuery(id+"F2.wireOp",EDGE,"E12"),sQuery(id+"F2.wireOp",EDGE,"E13"),sQuery(id+"F2.wireOp",EDGE,"E14")])],"isStart":false})});var subQ32=sQuery(id+"F17.wireOp",EDGE,"E32.right");var subQ33=makeQuery(id+"F18.opExtrude","SWEPT_FACE",FACE,{"disambiguationData":[OSD([subQ32])]});var subQ34=sQuery(id+"F10.wireOp",EDGE,"E19.right");var subQ35=sQuery(id+"F10.wireOp",EDGE,"E19.left");var subQ36=makeQuery(id+"F11.opExtrude","CAP_FACE",FACE,{"disambiguationData":[OSD([subQ19,sQuery(id+"F10.wireOp",EDGE,"E18.top"),subQ9,subQ18,subQ0,sQuery(id+"F10.wireOp",EDGE,"E19.top"),subQ35,subQ34,subQ23,sQuery(id+"F10.wireOp",EDGE,"E20.top"),sQuery(id+"F10.wireOp",EDGE,"E21.bottom"),sQuery(id+"F10.wireOp",EDGE,"E21.top"),sQuery(id+"F10.wireOp",EDGE,"E22.bottom"),sQuery(id+"F10.wireOp",EDGE,"E22.top"),sQuery(id+"F10.wireOp",EDGE,"E23.bottom"),sQuery(id+"F10.wireOp",EDGE,"E23.top"),sQuery(id+"F10.wireOp",EDGE,"E24.bottom"),sQuery(id+"F10.wireOp",EDGE,"E24.top")])],"isStart":false});var subQ37=makeQuery(id+"F18.opExtrude","CAP_FACE",FACE,{"disambiguationData":[OSD([sQuery(id+"F17.wireOp",EDGE,"E28.left"),sQuery(id+"F17.wireOp",EDGE,"E28.right"),sQuery(id+"F17.wireOp",EDGE,"E29.bottom"),sQuery(id+"F17.wireOp",EDGE,"E29.top"),sQuery(id+"F17.wireOp",EDGE,"E29.left"),sQuery(id+"F17.wireOp",EDGE,"E29.right"),sQuery(id+"F17.wireOp",EDGE,"E30.left"),sQuery(id+"F17.wireOp",EDGE,"E30.right"),sQuery(id+"F17.wireOp",EDGE,"E31.bottom"),sQuery(id+"F17.wireOp",EDGE,"E31.top"),sQuery(id+"F17.wireOp",EDGE,"E31.left"),sQuery(id+"F17.wireOp",EDGE,"E31.right"),subQ27,sQuery(id+"F17.wireOp",EDGE,"E32.top"),sQuery(id+"F17.wireOp",EDGE,"E32.left"),subQ32,subQ26,sQuery(id+"F17.wireOp",EDGE,"E33.top"),sQuery(id+"F17.wireOp",EDGE,"E33.left"),sQuery(id+"F17.wireOp",EDGE,"E33.right"),subQ25,sQuery(id+"F17.wireOp",EDGE,"E34.top"),sQuery(id+"F17.wireOp",EDGE,"E34.left"),sQuery(id+"F17.wireOp",EDGE,"E34.right")])],"isStart":false});var subQ38=makeQuery(id+"F1.opExtrude","CAP_FACE",FACE,{"disambiguationData":[OSD([subQ21,sQuery(id+"F0.wireOp",EDGE,"E0.top"),sQuery(id+"F0.wireOp",EDGE,"E0.left"),subQ20])],"isStart":false});var subQ39=makeQuery(id+"F11.opExtrude","SWEPT_FACE",FACE,{"disambiguationData":[OSD([subQ19])]});var subQ40=sQuery(id+"F25.wireOp",EDGE,"E44.left");var subQ41=makeQuery(id+"F26.opExtrude","SWEPT_FACE",FACE,{"disambiguationData":[OSD([subQ40])]});var subQ42=makeQuery(id+"F1.opExtrude","SWEPT_FACE",FACE,{"disambiguationData":[OSD([subQ20])]});var subQ43=makeQuery(id+"F42.opExtrude","SWEPT_FACE",FACE,{"disambiguationData":[OSD([sQuery(id+"F41.wireOp",EDGE,"E67.bottom")])]});var subQ44=makeQuery(id+"F40.opExtrude","SWEPT_FACE",FACE,{"disambiguationData":[OSD([sQuery(id+"F39.wireOp",EDGE,"E64.left")])]});var subQ45=sQuery(id+"F25.wireOp",EDGE,"E44.right");var subQ46=makeQuery(id+"F26.opExtrude","CAP_FACE",FACE,{"disambiguationData":[OSD([sQuery(id+"F25.wireOp",EDGE,"E41.left"),sQuery(id+"F25.wireOp",EDGE,"E41.right"),sQuery(id+"F25.wireOp",EDGE,"E42.left"),sQuery(id+"F25.wireOp",EDGE,"E42.right"),sQuery(id+"F25.wireOp",EDGE,"E43.bottom"),sQuery(id+"F25.wireOp",EDGE,"E43.top"),sQuery(id+"F25.wireOp",EDGE,"E43.left"),sQuery(id+"F25.wireOp",EDGE,"E43.right"),subQ29,sQuery(id+"F25.wireOp",EDGE,"E44.top"),subQ40,subQ45,sQuery(id+"F25.wireOp",EDGE,"E45.bottom"),sQuery(id+"F25.wireOp",EDGE,"E45.top"),sQuery(id+"F25.wireOp",EDGE,"E45.left"),sQuery(id+"F25.wireOp",EDGE,"E45.right"),sQuery(id+"F25.wireOp",EDGE,"E46.bottom"),sQuery(id+"F25.wireOp",EDGE,"E46.top"),sQuery(id+"F25.wireOp",EDGE,"E46.left"),sQuery(id+"F25.wireOp",EDGE,"E46.right")])],"isStart":false});var subQ47=makeQuery(id+"F11.opExtrude","SWEPT_FACE",FACE,{"disambiguationData":[OSD([subQ34])]});var subQ48=makeQuery(id+"F1.opExtrude","SWEPT_FACE",FACE,{"disambiguationData":[OSD([subQ21])]});var subQ49=makeQuery(id+"F11.opExtrude","SWEPT_FACE",FACE,{"disambiguationData":[OSD([subQ35]),TDD([makeQuery(id+"F10.imprint","IMPRINT",EDGE,{"disambiguationData":[TD([[makeQuery(id+"F10.imprint","INTERSECT",VERTEX,{"derivedFrom":[subQ35,subQ23,sQuery(id+"F10.wireOp",EDGE,"E20.right")]}),1.0]])],"derivedFrom":subQ35})])]});var subQ50=sQuery(id+"F37.wireOp",EDGE,"E57");var subQ51=makeQuery(id+"F38.boolean.opBoolean","COPY",FACE,{"derivedFrom":makeQuery(id+"F38.opExtrude","CAP_FACE",FACE,{"disambiguationData":[OSD([subQ21,subQ20,subQ50,sQuery(id+"F37.wireOp",EDGE,"E58"),sQuery(id+"F37.wireOp",EDGE,"E59"),sQuery(id+"F37.wireOp",EDGE,"E60"),sQuery(id+"F37.wireOp",EDGE,"E61"),sQuery(id+"F37.wireOp",EDGE,"E62")])],"isStart":false})});var subQ52=makeQuery(id+"F26.opExtrude","SWEPT_FACE",FACE,{"disambiguationData":[OSD([subQ45])]});var subQ53=makeQuery(id+"F38.boolean.opBoolean","COPY",FACE,{"derivedFrom":makeQuery(id+"F38.opExtrude","SWEPT_FACE",FACE,{"disambiguationData":[OSD([subQ50])]})});var subQ54=makeQuery(id+"F26.boolean.opBoolean","MERGE",FACE,{"derivedFrom":[makeQuery(id+"F18.boolean.opBoolean","MERGE",FACE,{"derivedFrom":[makeQuery(id+"F11.boolean.opBoolean","MERGE",FACE,{"derivedFrom":[subQ48,subQ39,subQ1]}),subQ28]}),subQ30]});Q0=makeQuery(id+"F76.boolean.opBoolean","SPLIT",FACE,{"disambiguationData":[TD([subQ48,subQ38,subQ42,subQ3,subQ31,subQ39,subQ36,subQ10,subQ24,subQ1,subQ49,subQ47,subQ37,subQ28,subQ33,subQ46,subQ30,subQ41,subQ52,subQ53,subQ51,subQ15,subQ17,subQ16,subQ44,subQ43,makeQuery(id+"F42.boolean.opBoolean","COPY",FACE,{"derivedFrom":makeQuery(id+"F42.opExtrude","SWEPT_FACE",FACE,{"disambiguationData":[OSD([sQuery(id+"F41.wireOp",EDGE,"E67.left")])]})}),makeQuery(id+"F42.boolean.opBoolean","COPY",FACE,{"derivedFrom":makeQuery(id+"F42.opExtrude","SWEPT_FACE",FACE,{"disambiguationData":[OSD([sQuery(id+"F41.wireOp",EDGE,"E67.right")])]})}),subQ14,subQ7,makeQuery(id+"F48.boolean.opBoolean","COPY",FACE,{"derivedFrom":makeQuery(id+"F48.opExtrude","CAP_FACE",FACE,{"disambiguationData":[OSD([sQuery(id+"F47.wireOp",EDGE,"E88.bottom"),subQ13,subQ12,subQ11])],"isStart":false})}),makeQuery(id+"F48.boolean.opBoolean","COPY",FACE,{"derivedFrom":makeQuery(id+"F48.opExtrude","SWEPT_FACE",FACE,{"disambiguationData":[OSD([subQ12])]})}),makeQuery(id+"F48.boolean.opBoolean","COPY",FACE,{"derivedFrom":makeQuery(id+"F48.opExtrude","SWEPT_FACE",FACE,{"disambiguationData":[OSD([subQ11])]})}),makeQuery(id+"F48.boolean.opBoolean","COPY",FACE,{"derivedFrom":makeQuery(id+"F48.opExtrude","CAP_FACE",FACE,{"disambiguationData":[OSD([sQuery(id+"F47.wireOp",EDGE,"E89.bottom"),subQ6,subQ5,subQ8])],"isStart":false})}),makeQuery(id+"F48.boolean.opBoolean","COPY",FACE,{"derivedFrom":makeQuery(id+"F48.opExtrude","SWEPT_FACE",FACE,{"disambiguationData":[OSD([subQ5])]})}),makeQuery(id+"F48.boolean.opBoolean","COPY",FACE,{"derivedFrom":makeQuery(id+"F48.opExtrude","SWEPT_FACE",FACE,{"disambiguationData":[OSD([subQ8])]})}),subQ4,makeQuery(id+"F52.opExtrude","SWEPT_FACE",FACE,{"disambiguationData":[OSD([sQuery(id+"F51.wireOp",EDGE,"E92.bottom")])]}),makeQuery(id+"F52.opExtrude","SWEPT_FACE",FACE,{"disambiguationData":[OSD([sQuery(id+"F51.wireOp",EDGE,"E92.left")])]}),makeQuery(id+"F52.opExtrude","SWEPT_FACE",FACE,{"disambiguationData":[OSD([sQuery(id+"F51.wireOp",EDGE,"E92.right")])]}),makeQuery(id+"F54.opExtrude","SWEPT_FACE",FACE,{"disambiguationData":[OSD([sQuery(id+"F53.wireOp",EDGE,"E93.right")])]}),makeQuery(id+"F56.opExtrude","SWEPT_FACE",FACE,{"disambiguationData":[OSD([sQuery(id+"F55.wireOp",EDGE,"E94.left")])]}),makeQuery(id+"F76.opExtrude","SWEPT_FACE",FACE,{"disambiguationData":[OSD([sQuery(id+"F75.wireOp",EDGE,"E120")])]}),makeQuery(id+"F76.opExtrude","SWEPT_FACE",FACE,{"disambiguationData":[OSD([sQuery(id+"F75.wireOp",EDGE,"E121")])]}),makeQuery(id+"F76.opExtrude","SWEPT_FACE",FACE,{"disambiguationData":[OSD([sQuery(id+"F75.wireOp",EDGE,"E122")])]}),makeQuery(id+"F76.opExtrude","SWEPT_FACE",FACE,{"disambiguationData":[OSD([sQuery(id+"F75.wireOp",EDGE,"E123")])]}),makeQuery(id+"F76.opExtrude","SWEPT_FACE",FACE,{"disambiguationData":[OSD([sQuery(id+"F75.wireOp",EDGE,"E124")])]}),makeQuery(id+"F76.opExtrude","SWEPT_FACE",FACE,{"disambiguationData":[OSD([sQuery(id+"F75.wireOp",EDGE,"E126")])]}),makeQuery(id+"F76.opExtrude","SWEPT_FACE",FACE,{"disambiguationData":[OSD([sQuery(id+"F75.wireOp",EDGE,"E127"),sQuery(id+"F75.wireOp",EDGE,"E128")])]}),makeQuery(id+"F76.opExtrude","SWEPT_FACE",FACE,{"disambiguationData":[OSD([sQuery(id+"F75.wireOp",EDGE,"E129")])]}),makeQuery(id+"F76.opExtrude","SWEPT_FACE",FACE,{"disambiguationData":[OSD([sQuery(id+"F75.wireOp",EDGE,"E130")])]}),makeQuery(id+"F76.opExtrude","SWEPT_FACE",FACE,{"disambiguationData":[OSD([sQuery(id+"F75.wireOp",EDGE,"E131")])]})])],"derivedFrom":makeQuery(id+"F50.boolean.opBoolean","MERGE",FACE,{"derivedFrom":[makeQuery(id+"F40.boolean.opBoolean","SPLIT",FACE,{"disambiguationData":[TD([makeQuery(id+"F40.opExtrude","SWEPT_FACE",FACE,{"disambiguationData":[OSD([sQuery(id+"F39.wireOp",EDGE,"E63.left")])]})])],"derivedFrom":subQ54}),makeQuery(id+"F48.boolean.opBoolean","MERGE",FACE,{"derivedFrom":[makeQuery(id+"F42.boolean.opBoolean","MERGE",FACE,{"derivedFrom":[makeQuery(id+"F40.boolean.opBoolean","SPLIT",FACE,{"disambiguationData":[TD([subQ42])],"derivedFrom":subQ54}),subQ43]}),subQ14,subQ7]}),subQ4]})});}
            var sketch = newSketch(context, id + "F113", { "sketchPlane" : qUnion([Q0])});
            skLineSegment(sketch, "E165.bottom", {"start": v(10.93, -5.53) * mm, "end": v(20.32, -5.53) * mm});
            skLineSegment(sketch, "E165.top", {"start": v(10.93, 4.52) * mm, "end": v(20.32, 4.52) * mm});
            skLineSegment(sketch, "E165.left", {"start": v(10.93, -5.53) * mm, "end": v(10.93, 4.52) * mm});
            skLineSegment(sketch, "E165.right", {"start": v(20.32, -5.53) * mm, "end": v(20.32, 4.52) * mm});
            skSolve(sketch);
        }
        {
            var Q0;
            Q0 = qSketchRegion(id + "F113", true);
            extrude(context, id + "F114", {"entities" : qUnion([Q0]), "operationType" : NewBodyOperationType.REMOVE, "oppositeDirection" : true, "depth" : 4.32 * mm, "offsetDistance" : 25.4 * mm});
        }
        {
            var Q0;
            Q0=makeQuery(id+"F18.boolean.opBoolean","MERGE",FACE,{"derivedFrom":[makeQuery(id+"F1.opExtrude","CAP_FACE",FACE,{"disambiguationData":[OSD([sQuery(id+"F0.wireOp",EDGE,"E0.bottom"),sQuery(id+"F0.wireOp",EDGE,"E0.top"),sQuery(id+"F0.wireOp",EDGE,"E0.left"),sQuery(id+"F0.wireOp",EDGE,"E0.right")])],"isStart":false}),makeQuery(id+"F18.opExtrude","SWEPT_FACE",FACE,{"disambiguationData":[OSD([sQuery(id+"F17.wireOp",EDGE,"E32.right")])]})]});
            var sketch = newSketch(context, id + "F115", { "sketchPlane" : qUnion([Q0])});
            skArc(sketch, "E166", {"start": v(-16.02, 8.54) * mm, "mid": v(-20.14, 12.66) * mm, "end": v(-24.26, 8.54) * mm});
            skSolve(sketch);
        }
        {
            var Q0;
            Q0 = qSketchRegion(id + "F115", true);
            var Q1;
            Q1=makeQuery(id+"F115.imprint","IMPRINT",FACE,{"disambiguationData":[TD([[makeQuery(id+"F115.imprint","IMPRINT",EDGE,{"derivedFrom":sQuery(id+"F115.wireOp",EDGE,"E166")}),1.0]])]});
            extrude(context, id + "F116", {"entities" : qUnion([Q0, Q1]), "operationType" : NewBodyOperationType.REMOVE, "oppositeDirection" : true, "depth" : 3.05 * mm, "offsetDistance" : 25.4 * mm});
        }
    });
